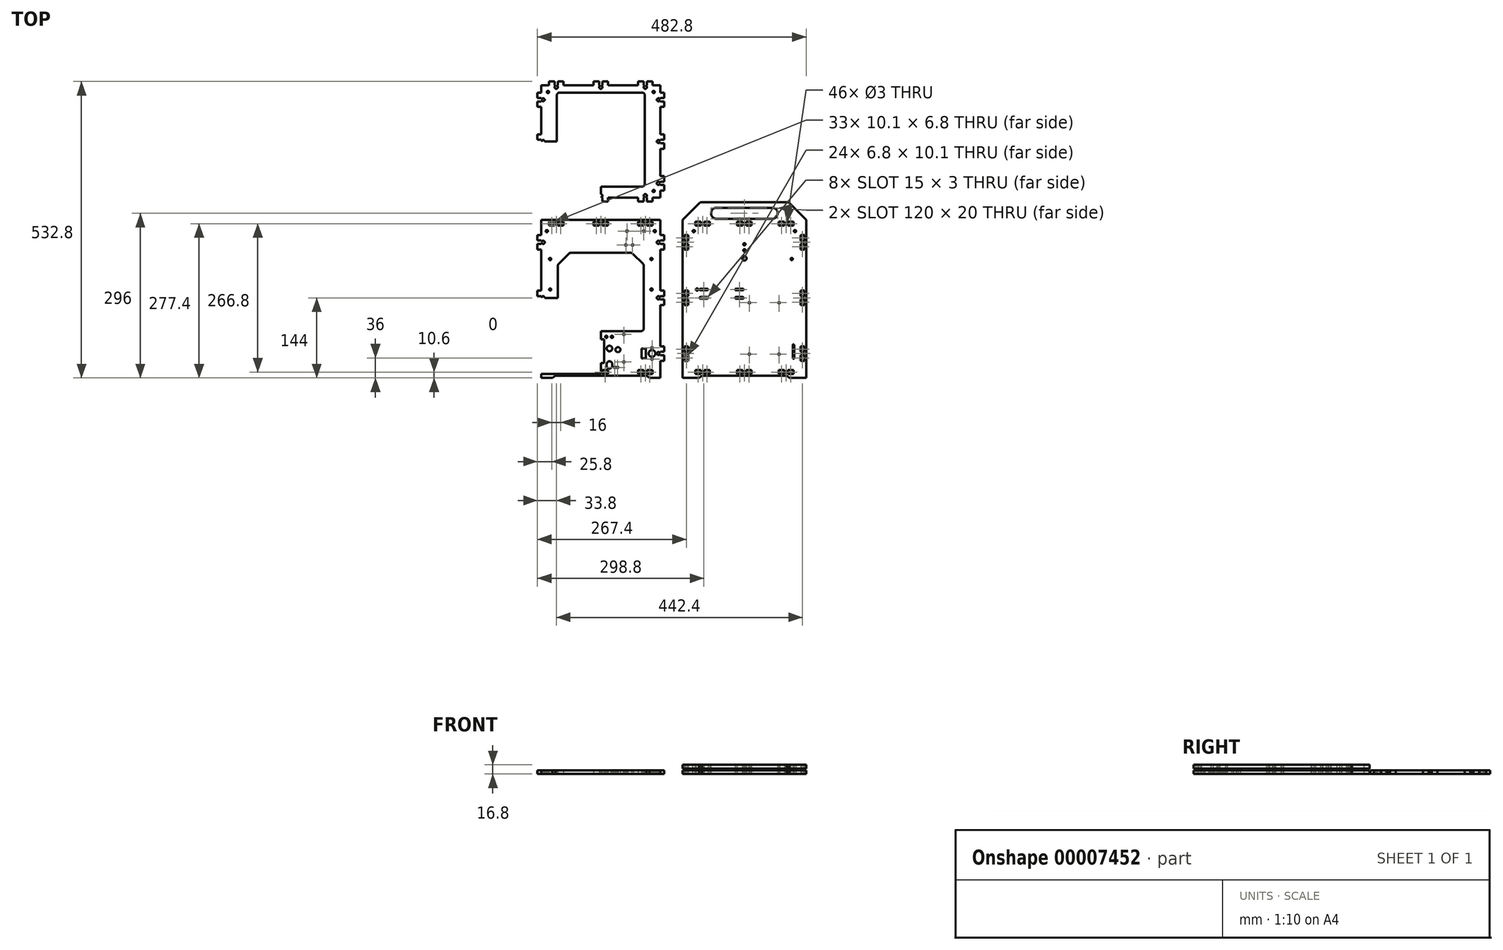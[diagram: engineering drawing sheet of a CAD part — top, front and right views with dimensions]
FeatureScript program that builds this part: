
annotation { "Feature Type Name" : "Feature", "Feature Type Description" : "" }
export const myFeature = defineFeature(function(context is Context, id is Id, definition is map)
    precondition{}
    {
        {
            var Q0;
            Q0=qCreatedBy(makeId("Top.planeOp"),FACE);
            var sketch = newSketch(context, id + "F0", { "sketchPlane" : qUnion([Q0])});
            skLineSegment(sketch, "E0", {"start": v(0, 0) * mm, "end": v(0, -101) * mm});
            skLineSegment(sketch, "E1", {"start": v(0, -101) * mm, "end": v(107, -101) * mm, "construction": true});
            skLineSegment(sketch, "E2", {"start": v(107, -101) * mm, "end": v(107, 101) * mm, "construction": true});
            skLineSegment(sketch, "E3", {"start": v(107, 101) * mm, "end": v(0, 101) * mm, "construction": true});
            skLineSegment(sketch, "E4", {"start": v(0, 101) * mm, "end": v(0, 0) * mm});
            skLineSegment(sketch, "E5", {"start": v(0, 0) * mm, "end": v(107, 0) * mm});
            skLineSegment(sketch, "E6", {"start": v(0, -101) * mm, "end": v(0, -151) * mm, "construction": true});
            skLineSegment(sketch, "E7", {"start": v(0, -151) * mm, "end": v(107, -151) * mm, "construction": true});
            skLineSegment(sketch, "E8", {"start": v(107, -151) * mm, "end": v(107, -411) * mm, "construction": true});
            skLineSegment(sketch, "E9", {"start": v(107, -411) * mm, "end": v(0, -411) * mm, "construction": true});
            skLineSegment(sketch, "E10", {"start": v(0, -411) * mm, "end": v(0, -151) * mm});
            skLineSegment(sketch, "E11", {"start": v(107, -151) * mm, "end": v(157, -151) * mm, "construction": true});
            skLineSegment(sketch, "E12", {"start": v(157, -151) * mm, "end": v(157, -411) * mm, "construction": true});
            skLineSegment(sketch, "E13", {"start": v(157, -411) * mm, "end": v(359, -411) * mm, "construction": true});
            skLineSegment(sketch, "E14", {"start": v(359, -411) * mm, "end": v(359, -151) * mm, "construction": true});
            skLineSegment(sketch, "E15", {"start": v(359, -151) * mm, "end": v(157, -151) * mm, "construction": true});
            skLineSegment(sketch, "E16", {"start": v(258, -151) * mm, "end": v(258, -411) * mm});
            skLineSegment(sketch, "E17", {"start": v(107, 0) * mm, "end": v(157, 0) * mm, "construction": true});
            skLineSegment(sketch, "E18", {"start": v(157, 0) * mm, "end": v(153.3, 0) * mm, "construction": true});
            skLineSegment(sketch, "E19", {"start": v(153.3, 0) * mm, "end": v(150.8, 0) * mm, "construction": true});
            skLineSegment(sketch, "E20", {"start": v(150.8, 0) * mm, "end": v(150.8, 1.5) * mm});
            skLineSegment(sketch, "E21", {"start": v(150.8, 1.5) * mm, "end": v(157, 1.5) * mm});
            skLineSegment(sketch, "E22", {"start": v(157, 1.5) * mm, "end": v(157, 3) * mm});
            skLineSegment(sketch, "E23", {"start": v(157, 3) * mm, "end": v(163.8, 3) * mm});
            skLineSegment(sketch, "E24", {"start": v(163.8, 3) * mm, "end": v(163.8, 13) * mm});
            skLineSegment(sketch, "E25", {"start": v(163.8, 13) * mm, "end": v(157, 13) * mm});
            skLineSegment(sketch, "E26.rect.bottom", {"start": v(154.5, 2.75) * mm, "end": v(152.1, 2.75) * mm});
            skLineSegment(sketch, "E26.rect.top", {"start": v(154.5, -2.75) * mm, "end": v(152.1, -2.75) * mm});
            skLineSegment(sketch, "E26.rect.left", {"start": v(154.5, 2.75) * mm, "end": v(154.5, -2.75) * mm});
            skLineSegment(sketch, "E26.rect.right", {"start": v(152.1, 2.75) * mm, "end": v(152.1, -2.75) * mm});
            skPoint(sketch, "E26.rect.middle", {"position": v(153.3, 0) * mm});
            skCircle(sketch, "E27", {"center": v(154.5, 2.75) * mm, "radius": 0.25 * mm});
            skLineSegment(sketch, "E28", {"start": v(157, 0) * mm, "end": v(187, 0) * mm, "construction": true});
            skLineSegment(sketch, "E29", {"start": v(187, 0) * mm, "end": v(187, 2.95) * mm, "construction": true});
            skLineSegment(sketch, "E30", {"start": v(187, 2.95) * mm, "end": v(193.8, 2.95) * mm});
            skLineSegment(sketch, "E31", {"start": v(193.8, 2.95) * mm, "end": v(193.8, 13.05) * mm});
            skLineSegment(sketch, "E32", {"start": v(193.8, 13.05) * mm, "end": v(187, 13.05) * mm});
            skLineSegment(sketch, "E33", {"start": v(187, 13.05) * mm, "end": v(187, 2.95) * mm});
            skLineSegment(sketch, "E34", {"start": v(187, 0) * mm, "end": v(190.4, 0) * mm, "construction": true});
            skLineSegment(sketch, "E35", {"start": v(190.4, 0) * mm, "end": v(190.4, 2.95) * mm, "construction": true});
            skCircle(sketch, "E36", {"center": v(190.4, 0) * mm, "radius": 1.5 * mm});
            skLineSegment(sketch, "E37", {"start": v(107, 0) * mm, "end": v(103.3, 0) * mm, "construction": true});
            skLineSegment(sketch, "E38", {"start": v(103.3, 0) * mm, "end": v(100.8, 0) * mm, "construction": true});
            skLineSegment(sketch, "E39", {"start": v(100.8, 0) * mm, "end": v(100.8, 1.5) * mm});
            skLineSegment(sketch, "E40", {"start": v(100.8, 1.5) * mm, "end": v(107, 1.5) * mm});
            skLineSegment(sketch, "E41", {"start": v(107, 1.5) * mm, "end": v(107, 3) * mm});
            skLineSegment(sketch, "E42", {"start": v(107, 3) * mm, "end": v(113.8, 3) * mm});
            skLineSegment(sketch, "E43", {"start": v(113.8, 3) * mm, "end": v(113.8, 13) * mm});
            skLineSegment(sketch, "E44", {"start": v(113.8, 13) * mm, "end": v(107, 13) * mm});
            skLineSegment(sketch, "E45.rect.bottom", {"start": v(104.5, 2.75) * mm, "end": v(102.1, 2.75) * mm});
            skLineSegment(sketch, "E45.rect.top", {"start": v(104.5, -2.75) * mm, "end": v(102.1, -2.75) * mm});
            skLineSegment(sketch, "E45.rect.left", {"start": v(104.5, 2.75) * mm, "end": v(104.5, -2.75) * mm});
            skLineSegment(sketch, "E45.rect.right", {"start": v(102.1, 2.75) * mm, "end": v(102.1, -2.75) * mm});
            skPoint(sketch, "E45.rect.middle", {"position": v(103.3, 0) * mm});
            skCircle(sketch, "E46", {"center": v(104.5, 2.75) * mm, "radius": 0.25 * mm});
            skLineSegment(sketch, "E47.0.MirrorCS", {"start": v(100.8, 0) * mm, "end": v(100.8, -1.5) * mm});
            skLineSegment(sketch, "E47.1.MirrorCS", {"start": v(107, -1.5) * mm, "end": v(107, -3) * mm});
            skCircle(sketch, "E47.2.MirrorC", {"center": v(104.5, -2.75) * mm, "radius": 0.25 * mm});
            skLineSegment(sketch, "E47.4.MirrorCS", {"start": v(113.8, -13) * mm, "end": v(107, -13) * mm});
            skLineSegment(sketch, "E47.6.MirrorCS", {"start": v(107, -3) * mm, "end": v(113.8, -3) * mm});
            skLineSegment(sketch, "E47.7.MirrorCS", {"start": v(100.8, -1.5) * mm, "end": v(107, -1.5) * mm});
            skLineSegment(sketch, "E47.8.MirrorCS", {"start": v(113.8, -3) * mm, "end": v(113.8, -13) * mm});
            skLineSegment(sketch, "E48", {"start": v(0, 101) * mm, "end": v(0, 97.3) * mm, "construction": true});
            skLineSegment(sketch, "E49", {"start": v(0, 97.3) * mm, "end": v(0, 94.8) * mm, "construction": true});
            skLineSegment(sketch, "E50", {"start": v(0, 94.8) * mm, "end": v(1.5, 94.8) * mm});
            skLineSegment(sketch, "E51", {"start": v(1.5, 94.8) * mm, "end": v(1.5, 101) * mm});
            skLineSegment(sketch, "E52", {"start": v(1.5, 101) * mm, "end": v(3, 101) * mm});
            skLineSegment(sketch, "E53", {"start": v(3, 101) * mm, "end": v(3, 107.8) * mm});
            skLineSegment(sketch, "E54", {"start": v(3, 107.8) * mm, "end": v(13, 107.8) * mm});
            skLineSegment(sketch, "E55", {"start": v(13, 107.8) * mm, "end": v(13, 101) * mm});
            skLineSegment(sketch, "E56.rect.bottom", {"start": v(2.75, 96.1) * mm, "end": v(-2.75, 96.1) * mm});
            skLineSegment(sketch, "E56.rect.top", {"start": v(2.75, 98.5) * mm, "end": v(-2.75, 98.5) * mm});
            skLineSegment(sketch, "E56.rect.left", {"start": v(2.75, 96.1) * mm, "end": v(2.75, 98.5) * mm});
            skLineSegment(sketch, "E56.rect.right", {"start": v(-2.75, 96.1) * mm, "end": v(-2.75, 98.5) * mm});
            skPoint(sketch, "E56.rect.middle", {"position": v(0, 97.3) * mm});
            skCircle(sketch, "E57", {"center": v(2.75, 98.5) * mm, "radius": 0.25 * mm});
            skLineSegment(sketch, "E58.0.MirrorCS", {"start": v(0, 94.8) * mm, "end": v(-1.5, 94.8) * mm});
            skCircle(sketch, "E58.1.MirrorC", {"center": v(-2.75, 98.5) * mm, "radius": 0.25 * mm});
            skLineSegment(sketch, "E58.3.MirrorCS", {"start": v(-1.5, 94.8) * mm, "end": v(-1.5, 101) * mm});
            skLineSegment(sketch, "E58.4.MirrorCS", {"start": v(-1.5, 101) * mm, "end": v(-3, 101) * mm});
            skLineSegment(sketch, "E58.5.MirrorCS", {"start": v(-3, 101) * mm, "end": v(-3, 107.8) * mm});
            skLineSegment(sketch, "E58.6.MirrorCS", {"start": v(-3, 107.8) * mm, "end": v(-13, 107.8) * mm});
            skLineSegment(sketch, "E58.7.MirrorCS", {"start": v(-13, 107.8) * mm, "end": v(-13, 101) * mm});
            skLineSegment(sketch, "E59", {"start": v(0, -281) * mm, "end": v(107, -281) * mm});
            skLineSegment(sketch, "E60", {"start": v(2.95, -151) * mm, "end": v(2.95, -144.2) * mm});
            skLineSegment(sketch, "E61", {"start": v(2.95, -144.2) * mm, "end": v(13.05, -144.2) * mm});
            skLineSegment(sketch, "E62", {"start": v(13.05, -144.2) * mm, "end": v(13.05, -151) * mm});
            skLineSegment(sketch, "E63", {"start": v(13.05, -151) * mm, "end": v(2.95, -151) * mm});
            skLineSegment(sketch, "E64", {"start": v(2.95, -147.6) * mm, "end": v(0, -147.6) * mm, "construction": true});
            skCircle(sketch, "E65", {"center": v(0, -147.6) * mm, "radius": 1.5 * mm});
            skLineSegment(sketch, "E66.0.MirrorCS", {"start": v(-13.05, -144.2) * mm, "end": v(-13.05, -151) * mm});
            skLineSegment(sketch, "E66.1.MirrorCS", {"start": v(-2.95, -151) * mm, "end": v(-2.95, -144.2) * mm});
            skLineSegment(sketch, "E66.2.MirrorCS", {"start": v(-13.05, -151) * mm, "end": v(-2.95, -151) * mm});
            skLineSegment(sketch, "E66.3.MirrorCS", {"start": v(-2.95, -144.2) * mm, "end": v(-13.05, -144.2) * mm});
            skLineSegment(sketch, "E67", {"start": v(260.95, -151) * mm, "end": v(260.95, -144.2) * mm});
            skLineSegment(sketch, "E68", {"start": v(260.95, -144.2) * mm, "end": v(271.05, -144.2) * mm});
            skLineSegment(sketch, "E69", {"start": v(271.05, -144.2) * mm, "end": v(271.05, -151) * mm});
            skLineSegment(sketch, "E70", {"start": v(271.05, -151) * mm, "end": v(260.95, -151) * mm});
            skLineSegment(sketch, "E71", {"start": v(260.95, -147.6) * mm, "end": v(258, -147.6) * mm, "construction": true});
            skLineSegment(sketch, "E72", {"start": v(258, -147.6) * mm, "end": v(258, -151) * mm, "construction": true});
            skCircle(sketch, "E73", {"center": v(258, -147.6) * mm, "radius": 1.5 * mm});
            skLineSegment(sketch, "E74.0.MirrorCS", {"start": v(244.95, -151) * mm, "end": v(255.05, -151) * mm});
            skLineSegment(sketch, "E74.1.MirrorCS", {"start": v(244.95, -144.2) * mm, "end": v(244.95, -151) * mm});
            skLineSegment(sketch, "E74.2.MirrorCS", {"start": v(255.05, -144.2) * mm, "end": v(244.95, -144.2) * mm});
            skLineSegment(sketch, "E74.3.MirrorCS", {"start": v(255.05, -151) * mm, "end": v(255.05, -144.2) * mm});
            skLineSegment(sketch, "E75", {"start": v(258, -281) * mm, "end": v(359, -281) * mm});
            skLineSegment(sketch, "E76", {"start": v(359, -278.05) * mm, "end": v(365.8, -278.05) * mm});
            skLineSegment(sketch, "E77", {"start": v(365.8, -278.05) * mm, "end": v(365.8, -267.95) * mm});
            skLineSegment(sketch, "E78", {"start": v(365.8, -267.95) * mm, "end": v(359, -267.95) * mm});
            skLineSegment(sketch, "E79", {"start": v(359, -267.95) * mm, "end": v(359, -278.05) * mm});
            skLineSegment(sketch, "E80", {"start": v(362.4, -278.05) * mm, "end": v(362.4, -281) * mm, "construction": true});
            skLineSegment(sketch, "E81", {"start": v(362.4, -281) * mm, "end": v(359, -281) * mm, "construction": true});
            skCircle(sketch, "E82", {"center": v(362.4, -281) * mm, "radius": 1.5 * mm});
            skLineSegment(sketch, "E83.0.MirrorCS", {"start": v(359, -294.05) * mm, "end": v(359, -283.95) * mm});
            skLineSegment(sketch, "E83.1.MirrorCS", {"start": v(359, -283.95) * mm, "end": v(365.8, -283.95) * mm});
            skLineSegment(sketch, "E83.2.MirrorCS", {"start": v(365.8, -294.05) * mm, "end": v(359, -294.05) * mm});
            skLineSegment(sketch, "E83.3.MirrorCS", {"start": v(365.8, -283.95) * mm, "end": v(365.8, -294.05) * mm});
            skLineSegment(sketch, "E84", {"start": v(107, -281) * mm, "end": v(103.3, -281) * mm, "construction": true});
            skLineSegment(sketch, "E85", {"start": v(103.3, -281) * mm, "end": v(100.8, -281) * mm, "construction": true});
            skLineSegment(sketch, "E86", {"start": v(100.8, -281) * mm, "end": v(100.8, -279.5) * mm});
            skLineSegment(sketch, "E87", {"start": v(100.8, -279.5) * mm, "end": v(107, -279.5) * mm});
            skLineSegment(sketch, "E88", {"start": v(107, -279.5) * mm, "end": v(107, -278) * mm});
            skLineSegment(sketch, "E89", {"start": v(107, -278) * mm, "end": v(113.8, -278) * mm});
            skLineSegment(sketch, "E90", {"start": v(113.8, -278) * mm, "end": v(113.8, -268) * mm});
            skLineSegment(sketch, "E91", {"start": v(113.8, -268) * mm, "end": v(107, -268) * mm});
            skLineSegment(sketch, "E92.rect.bottom", {"start": v(102.1, -278.25) * mm, "end": v(104.5, -278.25) * mm});
            skLineSegment(sketch, "E92.rect.top", {"start": v(102.1, -283.75) * mm, "end": v(104.5, -283.75) * mm});
            skLineSegment(sketch, "E92.rect.left", {"start": v(102.1, -278.25) * mm, "end": v(102.1, -283.75) * mm});
            skLineSegment(sketch, "E92.rect.right", {"start": v(104.5, -278.25) * mm, "end": v(104.5, -283.75) * mm});
            skPoint(sketch, "E92.rect.middle", {"position": v(103.3, -281) * mm});
            skCircle(sketch, "E93", {"center": v(104.5, -278.25) * mm, "radius": 0.25 * mm});
            skLineSegment(sketch, "E94.0.MirrorCS", {"start": v(100.8, -281) * mm, "end": v(100.8, -282.5) * mm});
            skCircle(sketch, "E94.1.MirrorC", {"center": v(104.5, -283.75) * mm, "radius": 0.25 * mm});
            skLineSegment(sketch, "E94.2.MirrorCS", {"start": v(100.8, -282.5) * mm, "end": v(107, -282.5) * mm});
            skLineSegment(sketch, "E94.4.MirrorCS", {"start": v(107, -284) * mm, "end": v(113.8, -284) * mm});
            skLineSegment(sketch, "E94.5.MirrorCS", {"start": v(113.8, -284) * mm, "end": v(113.8, -294) * mm});
            skLineSegment(sketch, "E94.6.MirrorCS", {"start": v(113.8, -294) * mm, "end": v(107, -294) * mm});
            skLineSegment(sketch, "E94.7.MirrorCS", {"start": v(107, -282.5) * mm, "end": v(107, -284) * mm});
            skLineSegment(sketch, "E95.1.0.0", {"start": v(83, 107.8) * mm, "end": v(93, 107.8) * mm});
            skPoint(sketch, "E95.1.0.1", {"position": v(80, 97.3) * mm});
            skLineSegment(sketch, "E95.1.0.2", {"start": v(77, 107.8) * mm, "end": v(67, 107.8) * mm});
            skLineSegment(sketch, "E95.1.0.3", {"start": v(93, 107.8) * mm, "end": v(93, 101) * mm});
            skLineSegment(sketch, "E95.1.0.4", {"start": v(67, 107.8) * mm, "end": v(67, 101) * mm});
            skLineSegment(sketch, "E95.1.0.5", {"start": v(83, 101) * mm, "end": v(83, 107.8) * mm});
            skLineSegment(sketch, "E95.1.0.6", {"start": v(77, 101) * mm, "end": v(77, 107.8) * mm});
            skLineSegment(sketch, "E95.1.0.7", {"start": v(80, 94.8) * mm, "end": v(78.5, 94.8) * mm});
            skLineSegment(sketch, "E95.1.0.8", {"start": v(78.5, 94.8) * mm, "end": v(78.5, 101) * mm});
            skLineSegment(sketch, "E95.1.0.9", {"start": v(82.75, 96.1) * mm, "end": v(77.25, 96.1) * mm});
            skLineSegment(sketch, "E95.1.0.10", {"start": v(80, 94.8) * mm, "end": v(81.5, 94.8) * mm});
            skLineSegment(sketch, "E95.1.0.11", {"start": v(81.5, 94.8) * mm, "end": v(81.5, 101) * mm});
            skLineSegment(sketch, "E95.1.0.12", {"start": v(77.25, 96.1) * mm, "end": v(77.25, 98.5) * mm});
            skLineSegment(sketch, "E95.1.0.13", {"start": v(82.75, 98.5) * mm, "end": v(77.25, 98.5) * mm});
            skLineSegment(sketch, "E95.1.0.14", {"start": v(78.5, 101) * mm, "end": v(77, 101) * mm});
            skLineSegment(sketch, "E95.1.0.15", {"start": v(80, 97.3) * mm, "end": v(80, 94.8) * mm, "construction": true});
            skLineSegment(sketch, "E95.1.0.16", {"start": v(81.5, 101) * mm, "end": v(83, 101) * mm});
            skLineSegment(sketch, "E95.1.0.17", {"start": v(77.25, 96.1) * mm, "end": v(77.25, 98.5) * mm});
            skCircle(sketch, "E95.1.0.18", {"center": v(82.75, 98.5) * mm, "radius": 0.25 * mm});
            skLineSegment(sketch, "E95.1.0.19", {"start": v(82.75, 96.1) * mm, "end": v(82.75, 98.5) * mm});
            skCircle(sketch, "E95.1.0.20", {"center": v(77.25, 98.5) * mm, "radius": 0.25 * mm});
            skLineSegment(sketch, "E95.1.0.21", {"start": v(80, 101) * mm, "end": v(80, 97.3) * mm, "construction": true});
            skLineSegment(sketch, "E95.direction1", {"start": v(3, 107.8) * mm, "end": v(83, 107.8) * mm, "construction": true});
            skLineSegment(sketch, "E96.0.1.0", {"start": v(113.8, 62) * mm, "end": v(107, 62) * mm});
            skPoint(sketch, "E96.0.1.1", {"position": v(103.3, 75) * mm});
            skLineSegment(sketch, "E96.0.1.2", {"start": v(113.8, 72) * mm, "end": v(113.8, 62) * mm});
            skLineSegment(sketch, "E96.0.1.3", {"start": v(107, 78) * mm, "end": v(113.8, 78) * mm});
            skLineSegment(sketch, "E96.0.1.4", {"start": v(107, 72) * mm, "end": v(113.8, 72) * mm});
            skLineSegment(sketch, "E96.0.1.5", {"start": v(113.8, 88) * mm, "end": v(107, 88) * mm});
            skLineSegment(sketch, "E96.0.1.6", {"start": v(113.8, 78) * mm, "end": v(113.8, 88) * mm});
            skPoint(sketch, "E96.0.1.7", {"position": v(103.3, 75) * mm});
            skLineSegment(sketch, "E96.0.1.8", {"start": v(107, 75) * mm, "end": v(103.3, 75) * mm, "construction": true});
            skLineSegment(sketch, "E96.0.1.9", {"start": v(104.5, 77.75) * mm, "end": v(104.5, 72.25) * mm});
            skLineSegment(sketch, "E96.0.1.10", {"start": v(100.8, 73.5) * mm, "end": v(107, 73.5) * mm});
            skLineSegment(sketch, "E96.0.1.11", {"start": v(100.8, 76.5) * mm, "end": v(107, 76.5) * mm});
            skLineSegment(sketch, "E96.0.1.12", {"start": v(107, 76.5) * mm, "end": v(107, 78) * mm});
            skLineSegment(sketch, "E96.0.1.13", {"start": v(100.8, 75) * mm, "end": v(100.8, 76.5) * mm});
            skCircle(sketch, "E96.0.1.14", {"center": v(104.5, 77.75) * mm, "radius": 0.25 * mm});
            skLineSegment(sketch, "E96.0.1.15", {"start": v(104.5, 77.75) * mm, "end": v(102.1, 77.75) * mm});
            skLineSegment(sketch, "E96.0.1.16", {"start": v(102.1, 77.75) * mm, "end": v(102.1, 72.25) * mm});
            skLineSegment(sketch, "E96.0.1.17", {"start": v(100.8, 75) * mm, "end": v(100.8, 73.5) * mm});
            skLineSegment(sketch, "E96.0.1.18", {"start": v(104.5, 72.25) * mm, "end": v(102.1, 72.25) * mm});
            skLineSegment(sketch, "E96.0.1.19", {"start": v(104.5, 72.25) * mm, "end": v(102.1, 72.25) * mm});
            skCircle(sketch, "E96.0.1.20", {"center": v(104.5, 72.25) * mm, "radius": 0.25 * mm});
            skLineSegment(sketch, "E96.0.1.21", {"start": v(103.3, 75) * mm, "end": v(100.8, 75) * mm, "construction": true});
            skLineSegment(sketch, "E96.0.1.22", {"start": v(107, 73.5) * mm, "end": v(107, 72) * mm});
            skLineSegment(sketch, "E96.direction1", {"start": v(107, -13) * mm, "end": v(132, -13) * mm, "construction": true});
            skLineSegment(sketch, "E96.direction2", {"start": v(107, -13) * mm, "end": v(107, 62) * mm, "construction": true});
            skLineSegment(sketch, "E97.1.0.0", {"start": v(66.95, -144.2) * mm, "end": v(66.95, -151) * mm});
            skLineSegment(sketch, "E97.1.0.1", {"start": v(66.95, -151) * mm, "end": v(77.05, -151) * mm});
            skLineSegment(sketch, "E97.1.0.2", {"start": v(77.05, -151) * mm, "end": v(77.05, -144.2) * mm});
            skLineSegment(sketch, "E97.1.0.3", {"start": v(77.05, -144.2) * mm, "end": v(66.95, -144.2) * mm});
            skCircle(sketch, "E97.1.0.4", {"center": v(80, -147.6) * mm, "radius": 1.5 * mm});
            skLineSegment(sketch, "E97.1.0.5", {"start": v(82.95, -144.2) * mm, "end": v(93.05, -144.2) * mm});
            skLineSegment(sketch, "E97.1.0.6", {"start": v(82.95, -151) * mm, "end": v(82.95, -144.2) * mm});
            skLineSegment(sketch, "E97.1.0.7", {"start": v(93.05, -151) * mm, "end": v(82.95, -151) * mm});
            skLineSegment(sketch, "E97.1.0.8", {"start": v(93.05, -144.2) * mm, "end": v(93.05, -151) * mm});
            skLineSegment(sketch, "E97.1.0.9", {"start": v(82.95, -147.6) * mm, "end": v(80, -147.6) * mm, "construction": true});
            skLineSegment(sketch, "E97.direction1", {"start": v(-13.05, -151) * mm, "end": v(66.95, -151) * mm, "construction": true});
            skPoint(sketch, "E98.0.1.0", {"position": v(103.3, -181) * mm});
            skLineSegment(sketch, "E98.0.1.1", {"start": v(113.8, -178) * mm, "end": v(113.8, -168) * mm});
            skLineSegment(sketch, "E98.0.1.2", {"start": v(113.8, -184) * mm, "end": v(113.8, -194) * mm});
            skLineSegment(sketch, "E98.0.1.3", {"start": v(113.8, -194) * mm, "end": v(107, -194) * mm});
            skLineSegment(sketch, "E98.0.1.4", {"start": v(113.8, -168) * mm, "end": v(107, -168) * mm});
            skPoint(sketch, "E98.0.1.5", {"position": v(103.3, -181) * mm});
            skLineSegment(sketch, "E98.0.1.6", {"start": v(107, -184) * mm, "end": v(113.8, -184) * mm});
            skLineSegment(sketch, "E98.0.1.7", {"start": v(107, -178) * mm, "end": v(113.8, -178) * mm});
            skLineSegment(sketch, "E98.0.1.8", {"start": v(102.1, -178.25) * mm, "end": v(104.5, -178.25) * mm});
            skLineSegment(sketch, "E98.0.1.9", {"start": v(104.5, -178.25) * mm, "end": v(104.5, -183.75) * mm});
            skLineSegment(sketch, "E98.0.1.10", {"start": v(100.8, -179.5) * mm, "end": v(107, -179.5) * mm});
            skLineSegment(sketch, "E98.0.1.11", {"start": v(100.8, -182.5) * mm, "end": v(107, -182.5) * mm});
            skLineSegment(sketch, "E98.0.1.12", {"start": v(107, -179.5) * mm, "end": v(107, -178) * mm});
            skLineSegment(sketch, "E98.0.1.13", {"start": v(107, -182.5) * mm, "end": v(107, -184) * mm});
            skLineSegment(sketch, "E98.0.1.14", {"start": v(107, -181) * mm, "end": v(103.3, -181) * mm, "construction": true});
            skLineSegment(sketch, "E98.0.1.15", {"start": v(102.1, -183.75) * mm, "end": v(104.5, -183.75) * mm});
            skCircle(sketch, "E98.0.1.16", {"center": v(104.5, -183.75) * mm, "radius": 0.25 * mm});
            skLineSegment(sketch, "E98.0.1.17", {"start": v(102.1, -178.25) * mm, "end": v(102.1, -183.75) * mm});
            skLineSegment(sketch, "E98.0.1.18", {"start": v(100.8, -181) * mm, "end": v(100.8, -182.5) * mm});
            skLineSegment(sketch, "E98.0.1.19", {"start": v(102.1, -183.75) * mm, "end": v(104.5, -183.75) * mm});
            skLineSegment(sketch, "E98.0.1.20", {"start": v(100.8, -181) * mm, "end": v(100.8, -179.5) * mm});
            skCircle(sketch, "E98.0.1.21", {"center": v(104.5, -178.25) * mm, "radius": 0.25 * mm});
            skLineSegment(sketch, "E98.0.1.22", {"start": v(103.3, -181) * mm, "end": v(100.8, -181) * mm, "construction": true});
            skLineSegment(sketch, "E98.direction1", {"start": v(103.3, -281) * mm, "end": v(128.76, -281) * mm, "construction": true});
            skLineSegment(sketch, "E98.direction2", {"start": v(103.3, -281) * mm, "end": v(103.3, -181) * mm, "construction": true});
            skLineSegment(sketch, "E99.1.0.0", {"start": v(346.05, -151) * mm, "end": v(335.95, -151) * mm});
            skLineSegment(sketch, "E99.1.0.1", {"start": v(335.95, -144.2) * mm, "end": v(346.05, -144.2) * mm});
            skLineSegment(sketch, "E99.1.0.2", {"start": v(319.95, -151) * mm, "end": v(330.05, -151) * mm});
            skLineSegment(sketch, "E99.1.0.3", {"start": v(330.05, -144.2) * mm, "end": v(319.95, -144.2) * mm});
            skLineSegment(sketch, "E99.1.0.4", {"start": v(346.05, -144.2) * mm, "end": v(346.05, -151) * mm});
            skLineSegment(sketch, "E99.1.0.5", {"start": v(319.95, -144.2) * mm, "end": v(319.95, -151) * mm});
            skLineSegment(sketch, "E99.1.0.6", {"start": v(330.05, -151) * mm, "end": v(330.05, -144.2) * mm});
            skLineSegment(sketch, "E99.1.0.7", {"start": v(335.95, -151) * mm, "end": v(335.95, -144.2) * mm});
            skCircle(sketch, "E99.1.0.8", {"center": v(333, -147.6) * mm, "radius": 1.5 * mm});
            skLineSegment(sketch, "E99.1.0.9", {"start": v(333, -147.6) * mm, "end": v(333, -151) * mm, "construction": true});
            skLineSegment(sketch, "E99.1.0.10", {"start": v(335.95, -147.6) * mm, "end": v(333, -147.6) * mm, "construction": true});
            skLineSegment(sketch, "E99.direction1", {"start": v(260.95, -151) * mm, "end": v(335.95, -151) * mm, "construction": true});
            skLineSegment(sketch, "E100.0.1.0", {"start": v(359, -167.95) * mm, "end": v(359, -178.05) * mm});
            skLineSegment(sketch, "E100.0.1.1", {"start": v(365.8, -178.05) * mm, "end": v(365.8, -167.95) * mm});
            skLineSegment(sketch, "E100.0.1.2", {"start": v(365.8, -167.95) * mm, "end": v(359, -167.95) * mm});
            skLineSegment(sketch, "E100.0.1.3", {"start": v(365.8, -194.05) * mm, "end": v(359, -194.05) * mm});
            skLineSegment(sketch, "E100.0.1.4", {"start": v(365.8, -183.95) * mm, "end": v(365.8, -194.05) * mm});
            skLineSegment(sketch, "E100.0.1.5", {"start": v(359, -194.05) * mm, "end": v(359, -183.95) * mm});
            skLineSegment(sketch, "E100.0.1.6", {"start": v(359, -178.05) * mm, "end": v(365.8, -178.05) * mm});
            skCircle(sketch, "E100.0.1.7", {"center": v(362.4, -181) * mm, "radius": 1.5 * mm});
            skLineSegment(sketch, "E100.0.1.8", {"start": v(362.4, -181) * mm, "end": v(359, -181) * mm, "construction": true});
            skLineSegment(sketch, "E100.0.1.9", {"start": v(359, -183.95) * mm, "end": v(365.8, -183.95) * mm});
            skLineSegment(sketch, "E100.0.1.10", {"start": v(362.4, -178.05) * mm, "end": v(362.4, -181) * mm, "construction": true});
            skLineSegment(sketch, "E100.direction1", {"start": v(359, -278.05) * mm, "end": v(459.05, -278.05) * mm, "construction": true});
            skLineSegment(sketch, "E100.direction2", {"start": v(359, -278.05) * mm, "end": v(359, -178.05) * mm, "construction": true});
            skLineSegment(sketch, "E101", {"start": v(107, -268) * mm, "end": v(107, -194) * mm});
            skLineSegment(sketch, "E102", {"start": v(107, -168) * mm, "end": v(107, -151) * mm});
            skLineSegment(sketch, "E103", {"start": v(107, -151) * mm, "end": v(107, -141) * mm});
            skLineSegment(sketch, "E104", {"start": v(107, -141) * mm, "end": v(0, -141) * mm});
            skLineSegment(sketch, "E105", {"start": v(0, -141) * mm, "end": v(0, -151) * mm});
            skLineSegment(sketch, "E106", {"start": v(359, -281) * mm, "end": v(369, -281) * mm});
            skLineSegment(sketch, "E107", {"start": v(369, -281) * mm, "end": v(369, -141) * mm});
            skLineSegment(sketch, "E108", {"start": v(369, -141) * mm, "end": v(258, -141) * mm});
            skLineSegment(sketch, "E109", {"start": v(258, -141) * mm, "end": v(258, -151) * mm});
            skLineSegment(sketch, "E110", {"start": v(13, 101) * mm, "end": v(67, 101) * mm});
            skLineSegment(sketch, "E111", {"start": v(93, 101) * mm, "end": v(107, 101) * mm});
            skLineSegment(sketch, "E112", {"start": v(107, 101) * mm, "end": v(107, 88) * mm});
            skLineSegment(sketch, "E113", {"start": v(107, 62) * mm, "end": v(107, 13) * mm});
            skLineSegment(sketch, "E114.0.MirrorCS", {"start": v(-107, -411) * mm, "end": v(0, -411) * mm, "construction": true});
            skLineSegment(sketch, "E114.1.MirrorCS", {"start": v(0, -151) * mm, "end": v(-107, -151) * mm, "construction": true});
            skLineSegment(sketch, "E114.2.MirrorCS", {"start": v(-107, -151) * mm, "end": v(-107, -411) * mm, "construction": true});
            skSolve(sketch);
        }
        {
            var Q0;
            Q0=qCreatedBy(makeId("Top.planeOp"),FACE);
            var sketch = newSketch(context, id + "F1", { "sketchPlane" : qUnion([Q0])});
            skLineSegment(sketch, "E115.0", {"start": v(0, -151) * mm, "end": v(-107, -151) * mm});
            skLineSegment(sketch, "E116.0", {"start": v(0, -151) * mm, "end": v(107, -151) * mm});
            skLineSegment(sketch, "E117.0", {"start": v(107, -151) * mm, "end": v(107, -411) * mm});
            skLineSegment(sketch, "E118.0", {"start": v(107, -411) * mm, "end": v(0, -411) * mm});
            skLineSegment(sketch, "E119.0", {"start": v(-107, -411) * mm, "end": v(0, -411) * mm});
            skLineSegment(sketch, "E120.0", {"start": v(-107, -151) * mm, "end": v(-107, -411) * mm});
            skLineSegment(sketch, "E121.0", {"start": v(157, -151) * mm, "end": v(157, -411) * mm});
            skLineSegment(sketch, "E122.0", {"start": v(157, -411) * mm, "end": v(359, -411) * mm});
            skLineSegment(sketch, "E123.0", {"start": v(359, -411) * mm, "end": v(359, -151) * mm});
            skLineSegment(sketch, "E124.0", {"start": v(359, -151) * mm, "end": v(157, -151) * mm});
            skLineSegment(sketch, "E125.0", {"start": v(0, -101) * mm, "end": v(107, -101) * mm});
            skLineSegment(sketch, "E126.0", {"start": v(107, -101) * mm, "end": v(107, 101) * mm});
            skLineSegment(sketch, "E127.0", {"start": v(107, 101) * mm, "end": v(0, 101) * mm});
            skLineSegment(sketch, "E128", {"start": v(258, -151) * mm, "end": v(258, -139) * mm});
            skLineSegment(sketch, "E129", {"start": v(258, -139) * mm, "end": v(308, -139) * mm});
            skLineSegment(sketch, "E130", {"start": v(308, -139) * mm, "end": v(308, -119) * mm});
            skLineSegment(sketch, "E131", {"start": v(308, -119) * mm, "end": v(258, -119) * mm});
            skLineSegment(sketch, "E132", {"start": v(258, -119) * mm, "end": v(258, -109) * mm});
            skLineSegment(sketch, "E133", {"start": v(258, -109) * mm, "end": v(334.93, -109) * mm});
            skLineSegment(sketch, "E134.0", {"start": v(369, -281) * mm, "end": v(369, -141) * mm});
            skLineSegment(sketch, "E135", {"start": v(338.46, -110.46) * mm, "end": v(369, -141) * mm});
            skLineSegment(sketch, "E136", {"start": v(369, -281) * mm, "end": v(369, -425) * mm});
            skLineSegment(sketch, "E137", {"start": v(369, -425) * mm, "end": v(339, -425) * mm});
            skLineSegment(sketch, "E138", {"start": v(339, -425) * mm, "end": v(334, -421) * mm});
            skLineSegment(sketch, "E139", {"start": v(334, -421) * mm, "end": v(258, -421) * mm});
            skLineSegment(sketch, "E140", {"start": v(258, -411) * mm, "end": v(258, -421) * mm});
            skLineSegment(sketch, "E141", {"start": v(0, -411) * mm, "end": v(0, -421) * mm});
            skLineSegment(sketch, "E142", {"start": v(0, -421) * mm, "end": v(82, -421) * mm});
            skLineSegment(sketch, "E143", {"start": v(82, -421) * mm, "end": v(87, -425) * mm});
            skLineSegment(sketch, "E144", {"start": v(87, -425) * mm, "end": v(107, -425) * mm});
            skLineSegment(sketch, "E145", {"start": v(107, -425) * mm, "end": v(107, -411) * mm});
            skLineSegment(sketch, "E146", {"start": v(107, -425) * mm, "end": v(369, -425) * mm, "construction": true});
            skLineSegment(sketch, "E147", {"start": v(0, -421) * mm, "end": v(258, -421) * mm, "construction": true});
            skLineSegment(sketch, "E148.0.MirrorCS", {"start": v(-82, -421) * mm, "end": v(-87, -425) * mm});
            skLineSegment(sketch, "E148.1.MirrorCS", {"start": v(0, -421) * mm, "end": v(-82, -421) * mm});
            skLineSegment(sketch, "E148.2.MirrorCS", {"start": v(-107, -425) * mm, "end": v(-107, -411) * mm});
            skLineSegment(sketch, "E148.3.MirrorCS", {"start": v(-87, -425) * mm, "end": v(-107, -425) * mm});
            skArc(sketch, "E149", {"start": v(308, -139) * mm, "mid": v(318, -129) * mm, "end": v(308, -119) * mm});
            skLineSegment(sketch, "E150.0.MirrorCS", {"start": v(182, -421) * mm, "end": v(258, -421) * mm});
            skLineSegment(sketch, "E150.1.MirrorCS", {"start": v(177, -425) * mm, "end": v(182, -421) * mm});
            skLineSegment(sketch, "E150.2.MirrorCS", {"start": v(147, -425) * mm, "end": v(177, -425) * mm});
            skLineSegment(sketch, "E150.3.MirrorCS", {"start": v(147, -281) * mm, "end": v(147, -425) * mm});
            skLineSegment(sketch, "E150.4.MirrorCS", {"start": v(177.54, -110.46) * mm, "end": v(147, -141) * mm});
            skLineSegment(sketch, "E150.5.MirrorCS", {"start": v(258, -109) * mm, "end": v(181.07, -109) * mm});
            skLineSegment(sketch, "E150.6.MirrorCS", {"start": v(208, -119) * mm, "end": v(258, -119) * mm});
            skLineSegment(sketch, "E150.7.MirrorCS", {"start": v(258, -139) * mm, "end": v(208, -139) * mm});
            skArc(sketch, "E150.8.MirrorCS", {"start": v(208, -139) * mm, "mid": v(198, -129) * mm, "end": v(208, -119) * mm});
            skLineSegment(sketch, "E151", {"start": v(147, -281) * mm, "end": v(147, -141) * mm});
            skLineSegment(sketch, "E152.0", {"start": v(260.95, -144.2) * mm, "end": v(271.05, -144.2) * mm});
            skLineSegment(sketch, "E153.0", {"start": v(365.8, -278.05) * mm, "end": v(365.8, -267.95) * mm});
            skLineSegment(sketch, "E154", {"start": v(258, -144.2) * mm, "end": v(365.8, -144.2) * mm});
            skLineSegment(sketch, "E155", {"start": v(365.8, -144.2) * mm, "end": v(365.8, -281) * mm});
            skLineSegment(sketch, "E156.0", {"start": v(258, -281) * mm, "end": v(359, -281) * mm});
            skLineSegment(sketch, "E157.0.MirrorCS", {"start": v(150.2, -144.2) * mm, "end": v(150.2, -281) * mm});
            skLineSegment(sketch, "E157.1.MirrorCS", {"start": v(258, -144.2) * mm, "end": v(150.2, -144.2) * mm});
            skLineSegment(sketch, "E158.0.MirrorCS", {"start": v(365.8, -417.8) * mm, "end": v(365.8, -281) * mm});
            skLineSegment(sketch, "E158.1.MirrorCS", {"start": v(258, -417.8) * mm, "end": v(365.8, -417.8) * mm});
            skLineSegment(sketch, "E158.2.MirrorCS", {"start": v(150.2, -417.8) * mm, "end": v(150.2, -281) * mm});
            skLineSegment(sketch, "E158.3.MirrorCS", {"start": v(258, -417.8) * mm, "end": v(150.2, -417.8) * mm});
            skLineSegment(sketch, "E159.0", {"start": v(2.95, -144.2) * mm, "end": v(13.05, -144.2) * mm});
            skLineSegment(sketch, "E160", {"start": v(0, -144.2) * mm, "end": v(107, -144.2) * mm});
            skLineSegment(sketch, "E161.0", {"start": v(0, -281) * mm, "end": v(107, -281) * mm});
            skLineSegment(sketch, "E162", {"start": v(107, -144.2) * mm, "end": v(107, -151) * mm});
            skLineSegment(sketch, "E163", {"start": v(107, -411) * mm, "end": v(107, -417.8) * mm});
            skLineSegment(sketch, "E164", {"start": v(107, -417.8) * mm, "end": v(-107, -417.8) * mm});
            skPoint(sketch, "E165.visualSharp", {"position": v(147, -141) * mm});
            skPoint(sketch, "E166.visualSharp", {"position": v(179, -109) * mm});
            skArc(sketch, "E166.filletArc", {"start": v(181.07, -109) * mm, "mid": v(179.16, -109.38) * mm, "end": v(177.54, -110.46) * mm});
            skPoint(sketch, "E167.visualSharp", {"position": v(337, -109) * mm});
            skArc(sketch, "E167.filletArc", {"start": v(338.46, -110.46) * mm, "mid": v(336.84, -109.38) * mm, "end": v(334.93, -109) * mm});
            skPoint(sketch, "E168.visualSharp", {"position": v(369, -141) * mm});
            skSolve(sketch);
        }
        {
            var Q0;
            Q0=qCreatedBy(makeId("Top.planeOp"),FACE);
            var sketch = newSketch(context, id + "F2", { "sketchPlane" : qUnion([Q0])});
            skLineSegment(sketch, "E169.rect.bottom", {"start": v(74, 88) * mm, "end": v(-74, 88) * mm});
            skLineSegment(sketch, "E169.rect.top", {"start": v(74, -81) * mm, "end": v(-74, -81) * mm});
            skLineSegment(sketch, "E169.rect.left", {"start": v(79, 83) * mm, "end": v(79, -76) * mm});
            skLineSegment(sketch, "E169.rect.right", {"start": v(-79, 83) * mm, "end": v(-79, -76) * mm});
            skPoint(sketch, "E169.rect.middle", {"position": v(0, 3.5) * mm});
            skCircle(sketch, "E170", {"center": v(30, -243) * mm, "radius": 1.5 * mm});
            skCircle(sketch, "E171", {"center": v(25, -406) * mm, "radius": 1.5 * mm});
            skCircle(sketch, "E172", {"center": v(30, -406) * mm, "radius": 1.5 * mm});
            skCircle(sketch, "E173", {"center": v(97, -161) * mm, "radius": 2 * mm});
            skCircle(sketch, "E174", {"center": v(95, -89) * mm, "radius": 2 * mm});
            skCircle(sketch, "E175", {"center": v(95, 89) * mm, "radius": 2 * mm});
            skCircle(sketch, "E176", {"center": v(167, -161) * mm, "radius": 2 * mm});
            skCircle(sketch, "E177", {"center": v(349, -161) * mm, "radius": 2 * mm});
            skCircle(sketch, "E178", {"center": v(173, -266) * mm, "radius": 2 * mm});
            skCircle(sketch, "E179", {"center": v(343, -211.2) * mm, "radius": 2 * mm});
            skLineSegment(sketch, "E180", {"start": v(179, -282.5) * mm, "end": v(179, -279.5) * mm});
            skLineSegment(sketch, "E181", {"start": v(179, -279.5) * mm, "end": v(191, -279.5) * mm});
            skLineSegment(sketch, "E182", {"start": v(191, -279.5) * mm, "end": v(191, -282.5) * mm});
            skLineSegment(sketch, "E183", {"start": v(191, -282.5) * mm, "end": v(179, -282.5) * mm});
            skArc(sketch, "E184", {"start": v(179, -279.5) * mm, "mid": v(177.5, -281) * mm, "end": v(179, -282.5) * mm});
            skArc(sketch, "E185", {"start": v(191, -282.5) * mm, "mid": v(192.5, -281) * mm, "end": v(191, -279.5) * mm});
            skLineSegment(sketch, "E186.0", {"start": v(0, 101) * mm, "end": v(0, 0) * mm});
            skCircle(sketch, "E187.0.MirrorC", {"center": v(-95, -89) * mm, "radius": 2 * mm});
            skCircle(sketch, "E187.1.MirrorC", {"center": v(-95, 89) * mm, "radius": 2 * mm});
            skCircle(sketch, "E188", {"center": v(91, -266) * mm, "radius": 2 * mm});
            skLineSegment(sketch, "E189", {"start": v(91, -266) * mm, "end": v(173, -266) * mm, "construction": true});
            skArc(sketch, "E190.0.1.0", {"start": v(191, -267.5) * mm, "mid": v(192.5, -266) * mm, "end": v(191, -264.5) * mm});
            skLineSegment(sketch, "E190.0.1.1", {"start": v(191, -267.5) * mm, "end": v(179, -267.5) * mm});
            skLineSegment(sketch, "E190.0.1.2", {"start": v(179, -264.5) * mm, "end": v(191, -264.5) * mm});
            skLineSegment(sketch, "E190.0.1.3", {"start": v(179, -267.5) * mm, "end": v(179, -264.5) * mm});
            skArc(sketch, "E190.0.1.4", {"start": v(179, -264.5) * mm, "mid": v(177.5, -266) * mm, "end": v(179, -267.5) * mm});
            skLineSegment(sketch, "E190.0.1.5", {"start": v(191, -264.5) * mm, "end": v(191, -267.5) * mm});
            skArc(sketch, "E190.1.0.0", {"start": v(255, -282.5) * mm, "mid": v(256.5, -281) * mm, "end": v(255, -279.5) * mm});
            skLineSegment(sketch, "E190.1.0.1", {"start": v(255, -282.5) * mm, "end": v(243, -282.5) * mm});
            skLineSegment(sketch, "E190.1.0.2", {"start": v(243, -279.5) * mm, "end": v(255, -279.5) * mm});
            skLineSegment(sketch, "E190.1.0.3", {"start": v(243, -282.5) * mm, "end": v(243, -279.5) * mm});
            skArc(sketch, "E190.1.0.4", {"start": v(243, -279.5) * mm, "mid": v(241.5, -281) * mm, "end": v(243, -282.5) * mm});
            skLineSegment(sketch, "E190.1.0.5", {"start": v(255, -279.5) * mm, "end": v(255, -282.5) * mm});
            skArc(sketch, "E190.1.1.0", {"start": v(255, -267.5) * mm, "mid": v(256.5, -266) * mm, "end": v(255, -264.5) * mm});
            skLineSegment(sketch, "E190.1.1.1", {"start": v(255, -267.5) * mm, "end": v(243, -267.5) * mm});
            skLineSegment(sketch, "E190.1.1.2", {"start": v(243, -264.5) * mm, "end": v(255, -264.5) * mm});
            skLineSegment(sketch, "E190.1.1.3", {"start": v(243, -267.5) * mm, "end": v(243, -264.5) * mm});
            skArc(sketch, "E190.1.1.4", {"start": v(243, -264.5) * mm, "mid": v(241.5, -266) * mm, "end": v(243, -267.5) * mm});
            skLineSegment(sketch, "E190.1.1.5", {"start": v(255, -264.5) * mm, "end": v(255, -267.5) * mm});
            skLineSegment(sketch, "E190.direction1", {"start": v(191, -282.5) * mm, "end": v(255, -282.5) * mm, "construction": true});
            skLineSegment(sketch, "E190.direction2", {"start": v(191, -282.5) * mm, "end": v(191, -267.5) * mm, "construction": true});
            skCircle(sketch, "E191.0.MirrorC", {"center": v(-25, -406) * mm, "radius": 1.5 * mm});
            skCircle(sketch, "E191.1.MirrorC", {"center": v(-30, -406) * mm, "radius": 1.5 * mm});
            skCircle(sketch, "E191.2.MirrorC", {"center": v(-30, -243) * mm, "radius": 1.5 * mm});
            skCircle(sketch, "E192.0.MirrorC", {"center": v(-97, -161) * mm, "radius": 2 * mm});
            skCircle(sketch, "E192.1.MirrorC", {"center": v(-91, -266) * mm, "radius": 2 * mm});
            skLineSegment(sketch, "E193", {"start": v(173, -266) * mm, "end": v(179, -266) * mm, "construction": true});
            skLineSegment(sketch, "E194", {"start": v(263.04, -285.92) * mm, "end": v(263.04, -386) * mm, "construction": true});
            skLineSegment(sketch, "E195", {"start": v(263.04, -285.92) * mm, "end": v(324, -285.92) * mm, "construction": true});
            skLineSegment(sketch, "E196", {"start": v(324, -285.92) * mm, "end": v(324, -386) * mm, "construction": true});
            skLineSegment(sketch, "E197", {"start": v(324, -386) * mm, "end": v(263.04, -386) * mm, "construction": true});
            skLineSegment(sketch, "E198", {"start": v(266.85, -289.73) * mm, "end": v(266.85, -382.19) * mm, "construction": true});
            skLineSegment(sketch, "E199", {"start": v(266.85, -382.19) * mm, "end": v(320.2, -382.19) * mm, "construction": true});
            skLineSegment(sketch, "E200", {"start": v(320.2, -382.19) * mm, "end": v(320.2, -289.73) * mm, "construction": true});
            skLineSegment(sketch, "E201", {"start": v(320.2, -289.73) * mm, "end": v(266.85, -289.73) * mm, "construction": true});
            skCircle(sketch, "E202", {"center": v(266.85, -382.19) * mm, "radius": 1.5 * mm});
            skCircle(sketch, "E203", {"center": v(266.85, -289.73) * mm, "radius": 1.5 * mm});
            skCircle(sketch, "E204", {"center": v(320.2, -289.73) * mm, "radius": 1.5 * mm});
            skCircle(sketch, "E205", {"center": v(320.2, -382.19) * mm, "radius": 1.5 * mm});
            skLineSegment(sketch, "E206", {"start": v(92, -371) * mm, "end": v(92, -391) * mm, "construction": true});
            skCircle(sketch, "E207", {"center": v(92, -381) * mm, "radius": 6 * mm});
            skCircle(sketch, "E208", {"center": v(92, -371) * mm, "radius": 1.5 * mm});
            skCircle(sketch, "E209", {"center": v(92, -391) * mm, "radius": 1.5 * mm});
            skLineSegment(sketch, "E210.rect.bottom", {"start": v(81, -372) * mm, "end": v(73, -372) * mm});
            skLineSegment(sketch, "E210.rect.top", {"start": v(81, -390) * mm, "end": v(73, -390) * mm});
            skLineSegment(sketch, "E210.rect.left", {"start": v(81, -372) * mm, "end": v(81, -390) * mm});
            skLineSegment(sketch, "E210.rect.right", {"start": v(73, -372) * mm, "end": v(73, -390) * mm});
            skPoint(sketch, "E210.rect.middle", {"position": v(77, -381) * mm});
            skLineSegment(sketch, "E211", {"start": v(77, -381) * mm, "end": v(92, -381) * mm, "construction": true});
            skLineSegment(sketch, "E212.0", {"start": v(0, -411) * mm, "end": v(0, -151) * mm});
            skLineSegment(sketch, "E213", {"start": v(0, -411) * mm, "end": v(15.5, -411) * mm, "construction": true});
            skLineSegment(sketch, "E214", {"start": v(15.5, -411) * mm, "end": v(15.5, -403) * mm, "construction": true});
            skLineSegment(sketch, "E215", {"start": v(15.5, -403) * mm, "end": v(15.5, -372) * mm, "construction": true});
            skCircle(sketch, "E216", {"center": v(15.5, -372) * mm, "radius": 5 * mm});
            skCircle(sketch, "E217.0.MirrorC", {"center": v(-15.5, -372) * mm, "radius": 5 * mm});
            skCircle(sketch, "E218", {"center": v(10, -351) * mm, "radius": 2 * mm});
            skLineSegment(sketch, "E219", {"start": v(0, -351) * mm, "end": v(10, -351) * mm, "construction": true});
            skLineSegment(sketch, "E220", {"start": v(10, -351) * mm, "end": v(20, -351) * mm, "construction": true});
            skCircle(sketch, "E221", {"center": v(20, -351) * mm, "radius": 2 * mm});
            skCircle(sketch, "E222.0.MirrorC", {"center": v(-20, -351) * mm, "radius": 2 * mm});
            skCircle(sketch, "E222.1.MirrorC", {"center": v(-10, -351) * mm, "radius": 2 * mm});
            skLineSegment(sketch, "E223", {"start": v(10.5, -403) * mm, "end": v(20.5, -403) * mm});
            skLineSegment(sketch, "E224", {"start": v(20.5, -403) * mm, "end": v(20.5, -400) * mm});
            skLineSegment(sketch, "E225", {"start": v(20.5, -400) * mm, "end": v(10.5, -400) * mm});
            skLineSegment(sketch, "E226", {"start": v(10.5, -400) * mm, "end": v(10.5, -403) * mm});
            skArc(sketch, "E227", {"start": v(10.5, -403) * mm, "mid": v(15.5, -408) * mm, "end": v(20.5, -403) * mm});
            skArc(sketch, "E228", {"start": v(20.5, -400) * mm, "mid": v(15.5, -395) * mm, "end": v(10.5, -400) * mm});
            skLineSegment(sketch, "E229.0.MirrorCS", {"start": v(-20.5, -403) * mm, "end": v(-20.5, -400) * mm});
            skLineSegment(sketch, "E229.1.MirrorCS", {"start": v(-10.5, -400) * mm, "end": v(-10.5, -403) * mm});
            skArc(sketch, "E229.2.MirrorCS", {"start": v(-10.5, -403) * mm, "mid": v(-15.5, -408) * mm, "end": v(-20.5, -403) * mm});
            skArc(sketch, "E229.3.MirrorCS", {"start": v(-20.5, -400) * mm, "mid": v(-15.5, -395) * mm, "end": v(-10.5, -400) * mm});
            skLineSegment(sketch, "E230.0", {"start": v(258, -151) * mm, "end": v(258, -411) * mm});
            skCircle(sketch, "E231", {"center": v(258, -184.6) * mm, "radius": 2 * mm});
            skCircle(sketch, "E232", {"center": v(258, -195.4) * mm, "radius": 2 * mm});
            skCircle(sketch, "E233", {"center": v(258, -210) * mm, "radius": 4 * mm});
            skLineSegment(sketch, "E234.rect.bottom", {"start": v(15.5, -253) * mm, "end": v(-15.5, -253) * mm});
            skLineSegment(sketch, "E234.rect.top", {"start": v(15.5, -288) * mm, "end": v(-15.5, -288) * mm});
            skLineSegment(sketch, "E234.rect.left", {"start": v(15.5, -253) * mm, "end": v(15.5, -288) * mm});
            skLineSegment(sketch, "E234.rect.right", {"start": v(-15.5, -253) * mm, "end": v(-15.5, -288) * mm});
            skPoint(sketch, "E234.rect.middle", {"position": v(0, -270.5) * mm});
            skLineSegment(sketch, "E235", {"start": v(47, -161) * mm, "end": v(77, -161) * mm, "construction": true});
            skCircle(sketch, "E236", {"center": v(47, -161) * mm, "radius": 1.5 * mm});
            skCircle(sketch, "E237", {"center": v(77, -161) * mm, "radius": 1.5 * mm});
            skArc(sketch, "E238", {"start": v(58, -266) * mm, "mid": v(51, -259) * mm, "end": v(44, -266) * mm});
            skPoint(sketch, "E239.visualSharp", {"position": v(-79, 88) * mm});
            skArc(sketch, "E239.filletArc", {"start": v(-74, 88) * mm, "mid": v(-77.54, 86.54) * mm, "end": v(-79, 83) * mm});
            skPoint(sketch, "E240.visualSharp", {"position": v(79, 88) * mm});
            skArc(sketch, "E240.filletArc", {"start": v(79, 83) * mm, "mid": v(77.54, 86.54) * mm, "end": v(74, 88) * mm});
            skPoint(sketch, "E241.visualSharp", {"position": v(79, -81) * mm});
            skArc(sketch, "E241.filletArc", {"start": v(74, -81) * mm, "mid": v(77.54, -79.54) * mm, "end": v(79, -76) * mm});
            skPoint(sketch, "E242.visualSharp", {"position": v(-79, -81) * mm});
            skArc(sketch, "E242.filletArc", {"start": v(-79, -76) * mm, "mid": v(-77.54, -79.54) * mm, "end": v(-74, -81) * mm});
            skLineSegment(sketch, "E243", {"start": v(91, -266) * mm, "end": v(51, -266) * mm, "construction": true});
            skLineSegment(sketch, "E244", {"start": v(51, -266) * mm, "end": v(51, -186) * mm, "construction": true});
            skLineSegment(sketch, "E245", {"start": v(45, -226) * mm, "end": v(57, -226) * mm, "construction": true});
            skLineSegment(sketch, "E246", {"start": v(45, -186) * mm, "end": v(57, -186) * mm, "construction": true});
            skPoint(sketch, "E247", {"position": v(51, -226) * mm});
            skCircle(sketch, "E248", {"center": v(45, -186) * mm, "radius": 1.5 * mm});
            skCircle(sketch, "E249", {"center": v(57, -186) * mm, "radius": 1.5 * mm});
            skCircle(sketch, "E250", {"center": v(57, -226) * mm, "radius": 1.5 * mm});
            skCircle(sketch, "E251", {"center": v(45, -226) * mm, "radius": 1.5 * mm});
            skLineSegment(sketch, "E252.bottom", {"start": v(58, -266) * mm, "end": v(51, -266) * mm});
            skLineSegment(sketch, "E252.left", {"start": v(58, -266) * mm, "end": v(58, -276) * mm});
            skLineSegment(sketch, "E252.right", {"start": v(44, -266) * mm, "end": v(44, -276) * mm});
            skPoint(sketch, "E252.middle", {"position": v(51, -271) * mm});
            skArc(sketch, "E253", {"start": v(44, -276) * mm, "mid": v(51, -283) * mm, "end": v(58, -276) * mm});
            skSolve(sketch);
        }
        {
            var Q0;
            Q0=qCreatedBy(makeId("Top.planeOp"),FACE);
            var sketch = newSketch(context, id + "F3", { "sketchPlane" : qUnion([Q0])});
            skCircle(sketch, "E254.0", {"center": v(97, -161) * mm, "radius": 2 * mm});
            skCircle(sketch, "E255.0", {"center": v(167, -161) * mm, "radius": 2 * mm});
            skCircle(sketch, "E256.0", {"center": v(349, -161) * mm, "radius": 2 * mm});
            skCircle(sketch, "E257.0", {"center": v(343, -211.2) * mm, "radius": 2 * mm});
            skArc(sketch, "E258.0", {"start": v(255, -267.5) * mm, "mid": v(256.5, -266) * mm, "end": v(255, -264.5) * mm});
            skLineSegment(sketch, "E259.0", {"start": v(243, -264.5) * mm, "end": v(255, -264.5) * mm});
            skLineSegment(sketch, "E260.0", {"start": v(255, -267.5) * mm, "end": v(243, -267.5) * mm});
            skArc(sketch, "E261.0", {"start": v(243, -264.5) * mm, "mid": v(241.5, -266) * mm, "end": v(243, -267.5) * mm});
            skLineSegment(sketch, "E262.0", {"start": v(243, -279.5) * mm, "end": v(255, -279.5) * mm});
            skArc(sketch, "E263.0", {"start": v(243, -279.5) * mm, "mid": v(241.5, -281) * mm, "end": v(243, -282.5) * mm});
            skArc(sketch, "E264.0", {"start": v(255, -282.5) * mm, "mid": v(256.5, -281) * mm, "end": v(255, -279.5) * mm});
            skLineSegment(sketch, "E265.0", {"start": v(255, -282.5) * mm, "end": v(243, -282.5) * mm});
            skArc(sketch, "E266.0", {"start": v(191, -267.5) * mm, "mid": v(192.5, -266) * mm, "end": v(191, -264.5) * mm});
            skLineSegment(sketch, "E267.0", {"start": v(191, -267.5) * mm, "end": v(179, -267.5) * mm});
            skLineSegment(sketch, "E268.0", {"start": v(179, -264.5) * mm, "end": v(191, -264.5) * mm});
            skArc(sketch, "E269.0", {"start": v(179, -264.5) * mm, "mid": v(177.5, -266) * mm, "end": v(179, -267.5) * mm});
            skArc(sketch, "E270.0", {"start": v(179, -279.5) * mm, "mid": v(177.5, -281) * mm, "end": v(179, -282.5) * mm});
            skLineSegment(sketch, "E271.0", {"start": v(179, -279.5) * mm, "end": v(191, -279.5) * mm});
            skLineSegment(sketch, "E272.0", {"start": v(191, -282.5) * mm, "end": v(179, -282.5) * mm});
            skArc(sketch, "E273.0", {"start": v(191, -282.5) * mm, "mid": v(192.5, -281) * mm, "end": v(191, -279.5) * mm});
            skCircle(sketch, "E274.0", {"center": v(173, -266) * mm, "radius": 2 * mm});
            skLineSegment(sketch, "E275.rect.top", {"start": v(72, -341) * mm, "end": v(-72, -341) * mm});
            skLineSegment(sketch, "E275.rect.left", {"start": v(77, -223.07) * mm, "end": v(77, -336) * mm});
            skLineSegment(sketch, "E275.rect.right", {"start": v(-77, -223.07) * mm, "end": v(-77, -336) * mm});
            skPoint(sketch, "E275.rect.middle", {"position": v(0, -281) * mm});
            skLineSegment(sketch, "E276", {"start": v(-92, -356.76) * mm, "end": v(-92, -396.76) * mm, "construction": true});
            skLineSegment(sketch, "E277", {"start": v(-92, -396.76) * mm, "end": v(5, -396.76) * mm, "construction": true});
            skLineSegment(sketch, "E278", {"start": v(5, -396.76) * mm, "end": v(5, -356.76) * mm, "construction": true});
            skLineSegment(sketch, "E279", {"start": v(5, -356.76) * mm, "end": v(-92, -356.76) * mm, "construction": true});
            skCircle(sketch, "E280.0", {"center": v(-97, -161) * mm, "radius": 2 * mm});
            skLineSegment(sketch, "E281", {"start": v(343, -211.2) * mm, "end": v(0, -211.2) * mm, "construction": true});
            skCircle(sketch, "E282", {"center": v(91, -211.2) * mm, "radius": 2 * mm});
            skLineSegment(sketch, "E283", {"start": v(0, 0) * mm, "end": v(0, -211.2) * mm, "construction": true});
            skCircle(sketch, "E284.0.MirrorC", {"center": v(-91, -211.2) * mm, "radius": 2 * mm});
            skCircle(sketch, "E285", {"center": v(25, 73) * mm, "radius": 1.5 * mm});
            skCircle(sketch, "E286", {"center": v(30, 36) * mm, "radius": 1.5 * mm});
            skCircle(sketch, "E287", {"center": v(47, 60) * mm, "radius": 1.5 * mm});
            skCircle(sketch, "E288", {"center": v(47, 43) * mm, "radius": 1.5 * mm});
            skCircle(sketch, "E289.0.MirrorC", {"center": v(-30, 36) * mm, "radius": 1.5 * mm});
            skCircle(sketch, "E289.1.MirrorC", {"center": v(-25, 73) * mm, "radius": 1.5 * mm});
            skLineSegment(sketch, "E290", {"start": v(-106, -344) * mm, "end": v(44.04, -344) * mm, "construction": true});
            skLineSegment(sketch, "E291", {"start": v(44.04, -344) * mm, "end": v(44.04, -399) * mm, "construction": true});
            skLineSegment(sketch, "E292", {"start": v(44.04, -399) * mm, "end": v(-106, -399) * mm, "construction": true});
            skLineSegment(sketch, "E293", {"start": v(-106, -399) * mm, "end": v(-106, -344) * mm, "construction": true});
            skCircle(sketch, "E294", {"center": v(-103.25, -346.66) * mm, "radius": 1.5 * mm});
            skLineSegment(sketch, "E295.bottom", {"start": v(-103.25, -346.66) * mm, "end": v(41.54, -346.66) * mm, "construction": true});
            skLineSegment(sketch, "E295.top", {"start": v(-103.25, -396.25) * mm, "end": v(41.54, -396.25) * mm, "construction": true});
            skLineSegment(sketch, "E295.left", {"start": v(-103.25, -346.66) * mm, "end": v(-103.25, -396.25) * mm, "construction": true});
            skLineSegment(sketch, "E295.right", {"start": v(41.54, -346.66) * mm, "end": v(41.54, -396.25) * mm, "construction": true});
            skCircle(sketch, "E296", {"center": v(-103.25, -396.25) * mm, "radius": 1.5 * mm});
            skCircle(sketch, "E297", {"center": v(41.54, -346.66) * mm, "radius": 1.5 * mm});
            skCircle(sketch, "E298", {"center": v(41.54, -396.25) * mm, "radius": 1.5 * mm});
            skLineSegment(sketch, "E299.bottom", {"start": v(-92.5, -347) * mm, "end": v(5.5, -347) * mm, "construction": true});
            skLineSegment(sketch, "E299.top", {"start": v(-92.5, -407.5) * mm, "end": v(5.5, -407.5) * mm, "construction": true});
            skLineSegment(sketch, "E299.left", {"start": v(-92.5, -347) * mm, "end": v(-92.5, -407.5) * mm, "construction": true});
            skLineSegment(sketch, "E299.right", {"start": v(5.5, -347) * mm, "end": v(5.5, -407.5) * mm, "construction": true});
            skCircle(sketch, "E300", {"center": v(30.74, -374.2) * mm, "radius": 4.5 * mm});
            skPoint(sketch, "E301.visualSharp", {"position": v(-77, -221) * mm});
            skPoint(sketch, "E302.visualSharp", {"position": v(77, -221) * mm});
            skPoint(sketch, "E303.visualSharp", {"position": v(77, -341) * mm});
            skArc(sketch, "E303.filletArc", {"start": v(72, -341) * mm, "mid": v(75.54, -339.54) * mm, "end": v(77, -336) * mm});
            skPoint(sketch, "E304.visualSharp", {"position": v(-77, -341) * mm});
            skArc(sketch, "E304.filletArc", {"start": v(-77, -336) * mm, "mid": v(-75.54, -339.54) * mm, "end": v(-72, -341) * mm});
            skLineSegment(sketch, "E305", {"start": v(347.4, -389) * mm, "end": v(347.4, -366) * mm});
            skLineSegment(sketch, "E306", {"start": v(347.4, -366) * mm, "end": v(344.8, -366) * mm});
            skLineSegment(sketch, "E307", {"start": v(344.8, -366) * mm, "end": v(344.8, -389) * mm});
            skLineSegment(sketch, "E308", {"start": v(344.8, -389) * mm, "end": v(347.4, -389) * mm});
            skArc(sketch, "E309", {"start": v(347.4, -366) * mm, "mid": v(346.1, -364.7) * mm, "end": v(344.8, -366) * mm});
            skArc(sketch, "E310", {"start": v(344.8, -389) * mm, "mid": v(346.1, -390.3) * mm, "end": v(347.4, -389) * mm});
            skLineSegment(sketch, "E311", {"start": v(347.4, -389) * mm, "end": v(347.4, -399) * mm, "construction": true});
            skLineSegment(sketch, "E312", {"start": v(44.04, -399) * mm, "end": v(347.4, -399) * mm, "construction": true});
            skLineSegment(sketch, "E313.bottom", {"start": v(-93, -355.76) * mm, "end": v(6, -355.76) * mm});
            skLineSegment(sketch, "E313.top", {"start": v(-93, -397.76) * mm, "end": v(6, -397.76) * mm});
            skLineSegment(sketch, "E313.left", {"start": v(-93, -355.76) * mm, "end": v(-93, -397.76) * mm});
            skLineSegment(sketch, "E313.right", {"start": v(6, -355.76) * mm, "end": v(6, -397.76) * mm});
            skLineSegment(sketch, "E314", {"start": v(0, -200.2) * mm, "end": v(54.13, -200.2) * mm});
            skLineSegment(sketch, "E315", {"start": v(57.66, -201.66) * mm, "end": v(75.54, -219.54) * mm});
            skLineSegment(sketch, "E316", {"start": v(0, -200.2) * mm, "end": v(-54.13, -200.2) * mm});
            skLineSegment(sketch, "E317", {"start": v(-57.66, -201.66) * mm, "end": v(-75.54, -219.54) * mm});
            skArc(sketch, "E318.filletArc", {"start": v(-75.54, -219.54) * mm, "mid": v(-76.62, -221.16) * mm, "end": v(-77, -223.07) * mm});
            skPoint(sketch, "E319.visualSharp", {"position": v(-56.2, -200.2) * mm});
            skArc(sketch, "E319.filletArc", {"start": v(-54.13, -200.2) * mm, "mid": v(-56.04, -200.58) * mm, "end": v(-57.66, -201.66) * mm});
            skPoint(sketch, "E320.visualSharp", {"position": v(56.2, -200.2) * mm});
            skArc(sketch, "E320.filletArc", {"start": v(57.66, -201.66) * mm, "mid": v(56.04, -200.58) * mm, "end": v(54.13, -200.2) * mm});
            skArc(sketch, "E321.filletArc", {"start": v(77, -223.07) * mm, "mid": v(76.62, -221.16) * mm, "end": v(75.54, -219.54) * mm});
            skCircle(sketch, "E322.0", {"center": v(258, -184.6) * mm, "radius": 2 * mm});
            skCircle(sketch, "E323.0", {"center": v(258, -195.4) * mm, "radius": 2 * mm});
            skCircle(sketch, "E324.0", {"center": v(258, -210) * mm, "radius": 4 * mm});
            skCircle(sketch, "E325", {"center": v(30.24, -354.5) * mm, "radius": 6.5 * mm, "construction": true});
            skPoint(sketch, "E326", {"position": v(347.4, -377.5) * mm});
            skSolve(sketch);
        }
        {
            var Q0;
            {var subQ29=sQuery(id+"F0.wireOp",EDGE,"E39");Q0=makeQuery(id+"F0.imprint","IMPRINT",FACE,{"disambiguationData":[TD([[makeQuery(id+"F0.imprint","IMPRINT",EDGE,{"derivedFrom":subQ29}),1.0]])]});}
            var Q1;
            Q1=makeQuery(id+"F0.imprint","IMPRINT",FACE,{"disambiguationData":[TD([[makeQuery(id+"F0.imprint","IMPRINT",EDGE,{"derivedFrom":sQuery(id+"F0.wireOp",EDGE,"E60")}),1.0]])]});
            var Q2;
            Q2=makeQuery(id+"F0.imprint","IMPRINT",FACE,{"disambiguationData":[TD([[makeQuery(id+"F0.imprint","IMPRINT",EDGE,{"derivedFrom":sQuery(id+"F0.wireOp",EDGE,"E67")}),1.0]])]});
            extrude(context, id + "F4", {"entities" : qUnion([Q0, Q1, Q2]), "depth" : 6.8 * mm});
        }
        {
            var Q0;
            Q0=makeQuery(id+"F4.opExtrude","SWEPT_BODY",BODY,{"disambiguationData":[OSD([sQuery(id+"F0.wireOp",EDGE,"E4"),sQuery(id+"F0.wireOp",EDGE,"E5"),sQuery(id+"F0.wireOp",EDGE,"E39"),sQuery(id+"F0.wireOp",EDGE,"E40"),sQuery(id+"F0.wireOp",EDGE,"E41"),sQuery(id+"F0.wireOp",EDGE,"E42"),sQuery(id+"F0.wireOp",EDGE,"E43"),sQuery(id+"F0.wireOp",EDGE,"E44"),sQuery(id+"F0.wireOp",EDGE,"E45.rect.bottom"),sQuery(id+"F0.wireOp",EDGE,"E45.rect.left"),sQuery(id+"F0.wireOp",EDGE,"E45.rect.right"),sQuery(id+"F0.wireOp",EDGE,"E46"),sQuery(id+"F0.wireOp",EDGE,"E50"),sQuery(id+"F0.wireOp",EDGE,"E51"),sQuery(id+"F0.wireOp",EDGE,"E52"),sQuery(id+"F0.wireOp",EDGE,"E53"),sQuery(id+"F0.wireOp",EDGE,"E54"),sQuery(id+"F0.wireOp",EDGE,"E55"),sQuery(id+"F0.wireOp",EDGE,"E56.rect.bottom"),sQuery(id+"F0.wireOp",EDGE,"E56.rect.top"),sQuery(id+"F0.wireOp",EDGE,"E56.rect.left"),sQuery(id+"F0.wireOp",EDGE,"E57"),sQuery(id+"F0.wireOp",EDGE,"E95.1.0.0"),sQuery(id+"F0.wireOp",EDGE,"E95.1.0.2"),sQuery(id+"F0.wireOp",EDGE,"E95.1.0.3"),sQuery(id+"F0.wireOp",EDGE,"E95.1.0.4"),sQuery(id+"F0.wireOp",EDGE,"E95.1.0.5"),sQuery(id+"F0.wireOp",EDGE,"E95.1.0.6"),sQuery(id+"F0.wireOp",EDGE,"E95.1.0.7"),sQuery(id+"F0.wireOp",EDGE,"E95.1.0.8"),sQuery(id+"F0.wireOp",EDGE,"E95.1.0.9"),sQuery(id+"F0.wireOp",EDGE,"E95.1.0.10"),sQuery(id+"F0.wireOp",EDGE,"E95.1.0.11"),sQuery(id+"F0.wireOp",EDGE,"E95.1.0.13"),sQuery(id+"F0.wireOp",EDGE,"E95.1.0.14"),sQuery(id+"F0.wireOp",EDGE,"E95.1.0.16"),sQuery(id+"F0.wireOp",EDGE,"E95.1.0.17"),sQuery(id+"F0.wireOp",EDGE,"E95.1.0.18"),sQuery(id+"F0.wireOp",EDGE,"E95.1.0.19"),sQuery(id+"F0.wireOp",EDGE,"E95.1.0.20"),sQuery(id+"F0.wireOp",EDGE,"E96.0.1.0"),sQuery(id+"F0.wireOp",EDGE,"E96.0.1.2"),sQuery(id+"F0.wireOp",EDGE,"E96.0.1.3"),sQuery(id+"F0.wireOp",EDGE,"E96.0.1.4"),sQuery(id+"F0.wireOp",EDGE,"E96.0.1.5"),sQuery(id+"F0.wireOp",EDGE,"E96.0.1.6"),sQuery(id+"F0.wireOp",EDGE,"E96.0.1.9"),sQuery(id+"F0.wireOp",EDGE,"E96.0.1.10"),sQuery(id+"F0.wireOp",EDGE,"E96.0.1.11"),sQuery(id+"F0.wireOp",EDGE,"E96.0.1.12"),sQuery(id+"F0.wireOp",EDGE,"E96.0.1.13"),sQuery(id+"F0.wireOp",EDGE,"E96.0.1.14"),sQuery(id+"F0.wireOp",EDGE,"E96.0.1.15"),sQuery(id+"F0.wireOp",EDGE,"E96.0.1.16"),sQuery(id+"F0.wireOp",EDGE,"E96.0.1.17"),sQuery(id+"F0.wireOp",EDGE,"E96.0.1.19"),sQuery(id+"F0.wireOp",EDGE,"E96.0.1.20"),sQuery(id+"F0.wireOp",EDGE,"E96.0.1.22"),sQuery(id+"F0.wireOp",EDGE,"E110"),sQuery(id+"F0.wireOp",EDGE,"E111"),sQuery(id+"F0.wireOp",EDGE,"E112"),sQuery(id+"F0.wireOp",EDGE,"E113")])]});
            var Q1;
            Q1=makeQuery(id+"F4.opExtrude","SWEPT_BODY",BODY,{"disambiguationData":[OSD([sQuery(id+"F0.wireOp",EDGE,"E10"),sQuery(id+"F0.wireOp",EDGE,"E59"),sQuery(id+"F0.wireOp",EDGE,"E60"),sQuery(id+"F0.wireOp",EDGE,"E61"),sQuery(id+"F0.wireOp",EDGE,"E62"),sQuery(id+"F0.wireOp",EDGE,"E63"),sQuery(id+"F0.wireOp",EDGE,"E65"),sQuery(id+"F0.wireOp",EDGE,"E86"),sQuery(id+"F0.wireOp",EDGE,"E87"),sQuery(id+"F0.wireOp",EDGE,"E88"),sQuery(id+"F0.wireOp",EDGE,"E89"),sQuery(id+"F0.wireOp",EDGE,"E90"),sQuery(id+"F0.wireOp",EDGE,"E91"),sQuery(id+"F0.wireOp",EDGE,"E92.rect.bottom"),sQuery(id+"F0.wireOp",EDGE,"E92.rect.left"),sQuery(id+"F0.wireOp",EDGE,"E92.rect.right"),sQuery(id+"F0.wireOp",EDGE,"E93"),sQuery(id+"F0.wireOp",EDGE,"E97.1.0.0"),sQuery(id+"F0.wireOp",EDGE,"E97.1.0.1"),sQuery(id+"F0.wireOp",EDGE,"E97.1.0.2"),sQuery(id+"F0.wireOp",EDGE,"E97.1.0.3"),sQuery(id+"F0.wireOp",EDGE,"E97.1.0.4"),sQuery(id+"F0.wireOp",EDGE,"E97.1.0.5"),sQuery(id+"F0.wireOp",EDGE,"E97.1.0.6"),sQuery(id+"F0.wireOp",EDGE,"E97.1.0.7"),sQuery(id+"F0.wireOp",EDGE,"E97.1.0.8"),sQuery(id+"F0.wireOp",EDGE,"E98.0.1.1"),sQuery(id+"F0.wireOp",EDGE,"E98.0.1.2"),sQuery(id+"F0.wireOp",EDGE,"E98.0.1.3"),sQuery(id+"F0.wireOp",EDGE,"E98.0.1.4"),sQuery(id+"F0.wireOp",EDGE,"E98.0.1.6"),sQuery(id+"F0.wireOp",EDGE,"E98.0.1.7"),sQuery(id+"F0.wireOp",EDGE,"E98.0.1.8"),sQuery(id+"F0.wireOp",EDGE,"E98.0.1.9"),sQuery(id+"F0.wireOp",EDGE,"E98.0.1.10"),sQuery(id+"F0.wireOp",EDGE,"E98.0.1.11"),sQuery(id+"F0.wireOp",EDGE,"E98.0.1.12"),sQuery(id+"F0.wireOp",EDGE,"E98.0.1.13"),sQuery(id+"F0.wireOp",EDGE,"E98.0.1.16"),sQuery(id+"F0.wireOp",EDGE,"E98.0.1.17"),sQuery(id+"F0.wireOp",EDGE,"E98.0.1.18"),sQuery(id+"F0.wireOp",EDGE,"E98.0.1.19"),sQuery(id+"F0.wireOp",EDGE,"E98.0.1.20"),sQuery(id+"F0.wireOp",EDGE,"E98.0.1.21"),sQuery(id+"F0.wireOp",EDGE,"E101"),sQuery(id+"F0.wireOp",EDGE,"E102"),sQuery(id+"F0.wireOp",EDGE,"E103"),sQuery(id+"F0.wireOp",EDGE,"E104"),sQuery(id+"F0.wireOp",EDGE,"E105")])]});
            var Q2;
            Q2=qCreatedBy(makeId("Right.planeOp"),FACE);
            mirror(context, id + "F5", {"operationType" : NewBodyOperationType.ADD, "entities" : qUnion([Q0, Q1]), "mirrorPlane" : qUnion([Q2])});
        }
        {
            var Q0;
            Q0=makeQuery(id+"F4.opExtrude","SWEPT_BODY",BODY,{"disambiguationData":[OSD([sQuery(id+"F0.wireOp",EDGE,"E4"),sQuery(id+"F0.wireOp",EDGE,"E5"),sQuery(id+"F0.wireOp",EDGE,"E39"),sQuery(id+"F0.wireOp",EDGE,"E40"),sQuery(id+"F0.wireOp",EDGE,"E41"),sQuery(id+"F0.wireOp",EDGE,"E42"),sQuery(id+"F0.wireOp",EDGE,"E43"),sQuery(id+"F0.wireOp",EDGE,"E44"),sQuery(id+"F0.wireOp",EDGE,"E45.rect.bottom"),sQuery(id+"F0.wireOp",EDGE,"E45.rect.left"),sQuery(id+"F0.wireOp",EDGE,"E45.rect.right"),sQuery(id+"F0.wireOp",EDGE,"E46"),sQuery(id+"F0.wireOp",EDGE,"E50"),sQuery(id+"F0.wireOp",EDGE,"E51"),sQuery(id+"F0.wireOp",EDGE,"E52"),sQuery(id+"F0.wireOp",EDGE,"E53"),sQuery(id+"F0.wireOp",EDGE,"E54"),sQuery(id+"F0.wireOp",EDGE,"E55"),sQuery(id+"F0.wireOp",EDGE,"E56.rect.bottom"),sQuery(id+"F0.wireOp",EDGE,"E56.rect.top"),sQuery(id+"F0.wireOp",EDGE,"E56.rect.left"),sQuery(id+"F0.wireOp",EDGE,"E57"),sQuery(id+"F0.wireOp",EDGE,"E95.1.0.0"),sQuery(id+"F0.wireOp",EDGE,"E95.1.0.2"),sQuery(id+"F0.wireOp",EDGE,"E95.1.0.3"),sQuery(id+"F0.wireOp",EDGE,"E95.1.0.4"),sQuery(id+"F0.wireOp",EDGE,"E95.1.0.5"),sQuery(id+"F0.wireOp",EDGE,"E95.1.0.6"),sQuery(id+"F0.wireOp",EDGE,"E95.1.0.7"),sQuery(id+"F0.wireOp",EDGE,"E95.1.0.8"),sQuery(id+"F0.wireOp",EDGE,"E95.1.0.9"),sQuery(id+"F0.wireOp",EDGE,"E95.1.0.10"),sQuery(id+"F0.wireOp",EDGE,"E95.1.0.11"),sQuery(id+"F0.wireOp",EDGE,"E95.1.0.13"),sQuery(id+"F0.wireOp",EDGE,"E95.1.0.14"),sQuery(id+"F0.wireOp",EDGE,"E95.1.0.16"),sQuery(id+"F0.wireOp",EDGE,"E95.1.0.17"),sQuery(id+"F0.wireOp",EDGE,"E95.1.0.18"),sQuery(id+"F0.wireOp",EDGE,"E95.1.0.19"),sQuery(id+"F0.wireOp",EDGE,"E95.1.0.20"),sQuery(id+"F0.wireOp",EDGE,"E96.0.1.0"),sQuery(id+"F0.wireOp",EDGE,"E96.0.1.2"),sQuery(id+"F0.wireOp",EDGE,"E96.0.1.3"),sQuery(id+"F0.wireOp",EDGE,"E96.0.1.4"),sQuery(id+"F0.wireOp",EDGE,"E96.0.1.5"),sQuery(id+"F0.wireOp",EDGE,"E96.0.1.6"),sQuery(id+"F0.wireOp",EDGE,"E96.0.1.9"),sQuery(id+"F0.wireOp",EDGE,"E96.0.1.10"),sQuery(id+"F0.wireOp",EDGE,"E96.0.1.11"),sQuery(id+"F0.wireOp",EDGE,"E96.0.1.12"),sQuery(id+"F0.wireOp",EDGE,"E96.0.1.13"),sQuery(id+"F0.wireOp",EDGE,"E96.0.1.14"),sQuery(id+"F0.wireOp",EDGE,"E96.0.1.15"),sQuery(id+"F0.wireOp",EDGE,"E96.0.1.16"),sQuery(id+"F0.wireOp",EDGE,"E96.0.1.17"),sQuery(id+"F0.wireOp",EDGE,"E96.0.1.19"),sQuery(id+"F0.wireOp",EDGE,"E96.0.1.20"),sQuery(id+"F0.wireOp",EDGE,"E96.0.1.22"),sQuery(id+"F0.wireOp",EDGE,"E110"),sQuery(id+"F0.wireOp",EDGE,"E111"),sQuery(id+"F0.wireOp",EDGE,"E112"),sQuery(id+"F0.wireOp",EDGE,"E113")])]});
            var Q1;
            Q1=qCreatedBy(makeId("Front.planeOp"),FACE);
            mirror(context, id + "F6", {"operationType" : NewBodyOperationType.ADD, "entities" : qUnion([Q0]), "mirrorPlane" : qUnion([Q1])});
        }
        {
            var Q0;
            Q0=makeQuery(id+"F4.opExtrude","SWEPT_BODY",BODY,{"disambiguationData":[OSD([sQuery(id+"F0.wireOp",EDGE,"E10"),sQuery(id+"F0.wireOp",EDGE,"E59"),sQuery(id+"F0.wireOp",EDGE,"E60"),sQuery(id+"F0.wireOp",EDGE,"E61"),sQuery(id+"F0.wireOp",EDGE,"E62"),sQuery(id+"F0.wireOp",EDGE,"E63"),sQuery(id+"F0.wireOp",EDGE,"E65"),sQuery(id+"F0.wireOp",EDGE,"E86"),sQuery(id+"F0.wireOp",EDGE,"E87"),sQuery(id+"F0.wireOp",EDGE,"E88"),sQuery(id+"F0.wireOp",EDGE,"E89"),sQuery(id+"F0.wireOp",EDGE,"E90"),sQuery(id+"F0.wireOp",EDGE,"E91"),sQuery(id+"F0.wireOp",EDGE,"E92.rect.bottom"),sQuery(id+"F0.wireOp",EDGE,"E92.rect.left"),sQuery(id+"F0.wireOp",EDGE,"E92.rect.right"),sQuery(id+"F0.wireOp",EDGE,"E93"),sQuery(id+"F0.wireOp",EDGE,"E97.1.0.0"),sQuery(id+"F0.wireOp",EDGE,"E97.1.0.1"),sQuery(id+"F0.wireOp",EDGE,"E97.1.0.2"),sQuery(id+"F0.wireOp",EDGE,"E97.1.0.3"),sQuery(id+"F0.wireOp",EDGE,"E97.1.0.4"),sQuery(id+"F0.wireOp",EDGE,"E97.1.0.5"),sQuery(id+"F0.wireOp",EDGE,"E97.1.0.6"),sQuery(id+"F0.wireOp",EDGE,"E97.1.0.7"),sQuery(id+"F0.wireOp",EDGE,"E97.1.0.8"),sQuery(id+"F0.wireOp",EDGE,"E98.0.1.1"),sQuery(id+"F0.wireOp",EDGE,"E98.0.1.2"),sQuery(id+"F0.wireOp",EDGE,"E98.0.1.3"),sQuery(id+"F0.wireOp",EDGE,"E98.0.1.4"),sQuery(id+"F0.wireOp",EDGE,"E98.0.1.6"),sQuery(id+"F0.wireOp",EDGE,"E98.0.1.7"),sQuery(id+"F0.wireOp",EDGE,"E98.0.1.8"),sQuery(id+"F0.wireOp",EDGE,"E98.0.1.9"),sQuery(id+"F0.wireOp",EDGE,"E98.0.1.10"),sQuery(id+"F0.wireOp",EDGE,"E98.0.1.11"),sQuery(id+"F0.wireOp",EDGE,"E98.0.1.12"),sQuery(id+"F0.wireOp",EDGE,"E98.0.1.13"),sQuery(id+"F0.wireOp",EDGE,"E98.0.1.16"),sQuery(id+"F0.wireOp",EDGE,"E98.0.1.17"),sQuery(id+"F0.wireOp",EDGE,"E98.0.1.18"),sQuery(id+"F0.wireOp",EDGE,"E98.0.1.19"),sQuery(id+"F0.wireOp",EDGE,"E98.0.1.20"),sQuery(id+"F0.wireOp",EDGE,"E98.0.1.21"),sQuery(id+"F0.wireOp",EDGE,"E101"),sQuery(id+"F0.wireOp",EDGE,"E102"),sQuery(id+"F0.wireOp",EDGE,"E103"),sQuery(id+"F0.wireOp",EDGE,"E104"),sQuery(id+"F0.wireOp",EDGE,"E105")])]});
            var Q1;
            Q1=makeQuery(id+"F4.opExtrude","SWEPT_BODY",BODY,{"disambiguationData":[OSD([sQuery(id+"F0.wireOp",EDGE,"E16"),sQuery(id+"F0.wireOp",EDGE,"E67"),sQuery(id+"F0.wireOp",EDGE,"E68"),sQuery(id+"F0.wireOp",EDGE,"E69"),sQuery(id+"F0.wireOp",EDGE,"E70"),sQuery(id+"F0.wireOp",EDGE,"E73"),sQuery(id+"F0.wireOp",EDGE,"E75"),sQuery(id+"F0.wireOp",EDGE,"E76"),sQuery(id+"F0.wireOp",EDGE,"E77"),sQuery(id+"F0.wireOp",EDGE,"E78"),sQuery(id+"F0.wireOp",EDGE,"E79"),sQuery(id+"F0.wireOp",EDGE,"E82"),sQuery(id+"F0.wireOp",EDGE,"E99.1.0.0"),sQuery(id+"F0.wireOp",EDGE,"E99.1.0.1"),sQuery(id+"F0.wireOp",EDGE,"E99.1.0.2"),sQuery(id+"F0.wireOp",EDGE,"E99.1.0.3"),sQuery(id+"F0.wireOp",EDGE,"E99.1.0.4"),sQuery(id+"F0.wireOp",EDGE,"E99.1.0.5"),sQuery(id+"F0.wireOp",EDGE,"E99.1.0.6"),sQuery(id+"F0.wireOp",EDGE,"E99.1.0.7"),sQuery(id+"F0.wireOp",EDGE,"E99.1.0.8"),sQuery(id+"F0.wireOp",EDGE,"E100.0.1.0"),sQuery(id+"F0.wireOp",EDGE,"E100.0.1.1"),sQuery(id+"F0.wireOp",EDGE,"E100.0.1.2"),sQuery(id+"F0.wireOp",EDGE,"E100.0.1.3"),sQuery(id+"F0.wireOp",EDGE,"E100.0.1.4"),sQuery(id+"F0.wireOp",EDGE,"E100.0.1.5"),sQuery(id+"F0.wireOp",EDGE,"E100.0.1.6"),sQuery(id+"F0.wireOp",EDGE,"E100.0.1.7"),sQuery(id+"F0.wireOp",EDGE,"E100.0.1.9"),sQuery(id+"F0.wireOp",EDGE,"E106"),sQuery(id+"F0.wireOp",EDGE,"E107"),sQuery(id+"F0.wireOp",EDGE,"E108"),sQuery(id+"F0.wireOp",EDGE,"E109")])]});
            var Q2;
            {var subQ0=makeQuery(id+"F4.opExtrude","SWEPT_FACE",FACE,{"disambiguationData":[OSD([sQuery(id+"F0.wireOp",EDGE,"E59")])]});Q2=makeQuery(id+"F5.boolean.opBoolean","MERGE",FACE,{"derivedFrom":[subQ0,makeQuery(id+"F5.opPattern","COPY",FACE,{"derivedFrom":subQ0,"instanceName":"1"})]});}
            mirror(context, id + "F7", {"operationType" : NewBodyOperationType.ADD, "entities" : qUnion([Q0, Q1]), "mirrorPlane" : qUnion([Q2])});
        }
        {
            var Q0;
            Q0=makeQuery(id+"F4.opExtrude","SWEPT_BODY",BODY,{"disambiguationData":[OSD([sQuery(id+"F0.wireOp",EDGE,"E16"),sQuery(id+"F0.wireOp",EDGE,"E67"),sQuery(id+"F0.wireOp",EDGE,"E68"),sQuery(id+"F0.wireOp",EDGE,"E69"),sQuery(id+"F0.wireOp",EDGE,"E70"),sQuery(id+"F0.wireOp",EDGE,"E73"),sQuery(id+"F0.wireOp",EDGE,"E75"),sQuery(id+"F0.wireOp",EDGE,"E76"),sQuery(id+"F0.wireOp",EDGE,"E77"),sQuery(id+"F0.wireOp",EDGE,"E78"),sQuery(id+"F0.wireOp",EDGE,"E79"),sQuery(id+"F0.wireOp",EDGE,"E82"),sQuery(id+"F0.wireOp",EDGE,"E99.1.0.0"),sQuery(id+"F0.wireOp",EDGE,"E99.1.0.1"),sQuery(id+"F0.wireOp",EDGE,"E99.1.0.2"),sQuery(id+"F0.wireOp",EDGE,"E99.1.0.3"),sQuery(id+"F0.wireOp",EDGE,"E99.1.0.4"),sQuery(id+"F0.wireOp",EDGE,"E99.1.0.5"),sQuery(id+"F0.wireOp",EDGE,"E99.1.0.6"),sQuery(id+"F0.wireOp",EDGE,"E99.1.0.7"),sQuery(id+"F0.wireOp",EDGE,"E99.1.0.8"),sQuery(id+"F0.wireOp",EDGE,"E100.0.1.0"),sQuery(id+"F0.wireOp",EDGE,"E100.0.1.1"),sQuery(id+"F0.wireOp",EDGE,"E100.0.1.2"),sQuery(id+"F0.wireOp",EDGE,"E100.0.1.3"),sQuery(id+"F0.wireOp",EDGE,"E100.0.1.4"),sQuery(id+"F0.wireOp",EDGE,"E100.0.1.5"),sQuery(id+"F0.wireOp",EDGE,"E100.0.1.6"),sQuery(id+"F0.wireOp",EDGE,"E100.0.1.7"),sQuery(id+"F0.wireOp",EDGE,"E100.0.1.9"),sQuery(id+"F0.wireOp",EDGE,"E106"),sQuery(id+"F0.wireOp",EDGE,"E107"),sQuery(id+"F0.wireOp",EDGE,"E108"),sQuery(id+"F0.wireOp",EDGE,"E109")])]});
            var Q1;
            {var subQ0=makeQuery(id+"F4.opExtrude","SWEPT_FACE",FACE,{"disambiguationData":[OSD([sQuery(id+"F0.wireOp",EDGE,"E16"),sQuery(id+"F0.wireOp",EDGE,"E109")])]});Q1=makeQuery(id+"F7.boolean.opBoolean","MERGE",FACE,{"derivedFrom":[subQ0,makeQuery(id+"F7.opPattern","COPY",FACE,{"derivedFrom":subQ0,"instanceName":"1"})]});}
            mirror(context, id + "F8", {"operationType" : NewBodyOperationType.ADD, "entities" : qUnion([Q0]), "mirrorPlane" : qUnion([Q1])});
        }
        {
            var Q0;
            Q0=makeQuery(id+"F1.imprint","IMPRINT",FACE,{"disambiguationData":[TD([[makeQuery(id+"F1.imprint","IMPRINT",EDGE,{"derivedFrom":sQuery(id+"F1.wireOp",EDGE,"E132")}),1.0]])]});
            var Q1;
            {var subQ13=sQuery(id+"F1.wireOp",EDGE,"E129");Q1=makeQuery(id+"F1.imprint","IMPRINT",FACE,{"disambiguationData":[TD([[makeQuery(id+"F1.imprint","IMPRINT",EDGE,{"derivedFrom":subQ13}),-1.0]])]});}
            var Q2;
            {var subQ4=sQuery(id+"F1.wireOp",EDGE,"E142");Q2=makeQuery(id+"F1.imprint","IMPRINT",FACE,{"disambiguationData":[TD([[makeQuery(id+"F1.imprint","IMPRINT",EDGE,{"derivedFrom":subQ4}),1.0]])]});}
            var Q3;
            Q3=makeQuery(id+"F1.imprint","IMPRINT",FACE,{"disambiguationData":[TD([[makeQuery(id+"F1.imprint","IMPRINT",EDGE,{"derivedFrom":sQuery(id+"F1.wireOp",EDGE,"E148.0.MirrorCS")}),-1.0]])]});
            extrude(context, id + "F9", {"entities" : qUnion([Q0, Q1, Q2, Q3]), "operationType" : NewBodyOperationType.ADD, "depth" : 6.8 * mm});
        }
        {
            var Q0;
            Q0=makeQuery(id+"F4.opExtrude","SWEPT_BODY",BODY,{"disambiguationData":[OSD([sQuery(id+"F0.wireOp",EDGE,"E4"),sQuery(id+"F0.wireOp",EDGE,"E5"),sQuery(id+"F0.wireOp",EDGE,"E39"),sQuery(id+"F0.wireOp",EDGE,"E40"),sQuery(id+"F0.wireOp",EDGE,"E41"),sQuery(id+"F0.wireOp",EDGE,"E42"),sQuery(id+"F0.wireOp",EDGE,"E43"),sQuery(id+"F0.wireOp",EDGE,"E44"),sQuery(id+"F0.wireOp",EDGE,"E45.rect.bottom"),sQuery(id+"F0.wireOp",EDGE,"E45.rect.left"),sQuery(id+"F0.wireOp",EDGE,"E45.rect.right"),sQuery(id+"F0.wireOp",EDGE,"E46"),sQuery(id+"F0.wireOp",EDGE,"E50"),sQuery(id+"F0.wireOp",EDGE,"E51"),sQuery(id+"F0.wireOp",EDGE,"E52"),sQuery(id+"F0.wireOp",EDGE,"E53"),sQuery(id+"F0.wireOp",EDGE,"E54"),sQuery(id+"F0.wireOp",EDGE,"E55"),sQuery(id+"F0.wireOp",EDGE,"E56.rect.bottom"),sQuery(id+"F0.wireOp",EDGE,"E56.rect.top"),sQuery(id+"F0.wireOp",EDGE,"E56.rect.left"),sQuery(id+"F0.wireOp",EDGE,"E57"),sQuery(id+"F0.wireOp",EDGE,"E95.1.0.0"),sQuery(id+"F0.wireOp",EDGE,"E95.1.0.2"),sQuery(id+"F0.wireOp",EDGE,"E95.1.0.3"),sQuery(id+"F0.wireOp",EDGE,"E95.1.0.4"),sQuery(id+"F0.wireOp",EDGE,"E95.1.0.5"),sQuery(id+"F0.wireOp",EDGE,"E95.1.0.6"),sQuery(id+"F0.wireOp",EDGE,"E95.1.0.7"),sQuery(id+"F0.wireOp",EDGE,"E95.1.0.8"),sQuery(id+"F0.wireOp",EDGE,"E95.1.0.9"),sQuery(id+"F0.wireOp",EDGE,"E95.1.0.10"),sQuery(id+"F0.wireOp",EDGE,"E95.1.0.11"),sQuery(id+"F0.wireOp",EDGE,"E95.1.0.13"),sQuery(id+"F0.wireOp",EDGE,"E95.1.0.14"),sQuery(id+"F0.wireOp",EDGE,"E95.1.0.16"),sQuery(id+"F0.wireOp",EDGE,"E95.1.0.17"),sQuery(id+"F0.wireOp",EDGE,"E95.1.0.18"),sQuery(id+"F0.wireOp",EDGE,"E95.1.0.19"),sQuery(id+"F0.wireOp",EDGE,"E95.1.0.20"),sQuery(id+"F0.wireOp",EDGE,"E96.0.1.0"),sQuery(id+"F0.wireOp",EDGE,"E96.0.1.2"),sQuery(id+"F0.wireOp",EDGE,"E96.0.1.3"),sQuery(id+"F0.wireOp",EDGE,"E96.0.1.4"),sQuery(id+"F0.wireOp",EDGE,"E96.0.1.5"),sQuery(id+"F0.wireOp",EDGE,"E96.0.1.6"),sQuery(id+"F0.wireOp",EDGE,"E96.0.1.9"),sQuery(id+"F0.wireOp",EDGE,"E96.0.1.10"),sQuery(id+"F0.wireOp",EDGE,"E96.0.1.11"),sQuery(id+"F0.wireOp",EDGE,"E96.0.1.12"),sQuery(id+"F0.wireOp",EDGE,"E96.0.1.13"),sQuery(id+"F0.wireOp",EDGE,"E96.0.1.14"),sQuery(id+"F0.wireOp",EDGE,"E96.0.1.15"),sQuery(id+"F0.wireOp",EDGE,"E96.0.1.16"),sQuery(id+"F0.wireOp",EDGE,"E96.0.1.17"),sQuery(id+"F0.wireOp",EDGE,"E96.0.1.19"),sQuery(id+"F0.wireOp",EDGE,"E96.0.1.20"),sQuery(id+"F0.wireOp",EDGE,"E96.0.1.22"),sQuery(id+"F0.wireOp",EDGE,"E110"),sQuery(id+"F0.wireOp",EDGE,"E111"),sQuery(id+"F0.wireOp",EDGE,"E112"),sQuery(id+"F0.wireOp",EDGE,"E113")])]});
            var Q1;
            Q1=makeQuery(id+"F4.opExtrude","SWEPT_BODY",BODY,{"disambiguationData":[OSD([sQuery(id+"F0.wireOp",EDGE,"E10"),sQuery(id+"F0.wireOp",EDGE,"E59"),sQuery(id+"F0.wireOp",EDGE,"E60"),sQuery(id+"F0.wireOp",EDGE,"E61"),sQuery(id+"F0.wireOp",EDGE,"E62"),sQuery(id+"F0.wireOp",EDGE,"E63"),sQuery(id+"F0.wireOp",EDGE,"E65"),sQuery(id+"F0.wireOp",EDGE,"E86"),sQuery(id+"F0.wireOp",EDGE,"E87"),sQuery(id+"F0.wireOp",EDGE,"E88"),sQuery(id+"F0.wireOp",EDGE,"E89"),sQuery(id+"F0.wireOp",EDGE,"E90"),sQuery(id+"F0.wireOp",EDGE,"E91"),sQuery(id+"F0.wireOp",EDGE,"E92.rect.bottom"),sQuery(id+"F0.wireOp",EDGE,"E92.rect.left"),sQuery(id+"F0.wireOp",EDGE,"E92.rect.right"),sQuery(id+"F0.wireOp",EDGE,"E93"),sQuery(id+"F0.wireOp",EDGE,"E97.1.0.0"),sQuery(id+"F0.wireOp",EDGE,"E97.1.0.1"),sQuery(id+"F0.wireOp",EDGE,"E97.1.0.2"),sQuery(id+"F0.wireOp",EDGE,"E97.1.0.3"),sQuery(id+"F0.wireOp",EDGE,"E97.1.0.4"),sQuery(id+"F0.wireOp",EDGE,"E97.1.0.5"),sQuery(id+"F0.wireOp",EDGE,"E97.1.0.6"),sQuery(id+"F0.wireOp",EDGE,"E97.1.0.7"),sQuery(id+"F0.wireOp",EDGE,"E97.1.0.8"),sQuery(id+"F0.wireOp",EDGE,"E98.0.1.1"),sQuery(id+"F0.wireOp",EDGE,"E98.0.1.2"),sQuery(id+"F0.wireOp",EDGE,"E98.0.1.3"),sQuery(id+"F0.wireOp",EDGE,"E98.0.1.4"),sQuery(id+"F0.wireOp",EDGE,"E98.0.1.6"),sQuery(id+"F0.wireOp",EDGE,"E98.0.1.7"),sQuery(id+"F0.wireOp",EDGE,"E98.0.1.8"),sQuery(id+"F0.wireOp",EDGE,"E98.0.1.9"),sQuery(id+"F0.wireOp",EDGE,"E98.0.1.10"),sQuery(id+"F0.wireOp",EDGE,"E98.0.1.11"),sQuery(id+"F0.wireOp",EDGE,"E98.0.1.12"),sQuery(id+"F0.wireOp",EDGE,"E98.0.1.13"),sQuery(id+"F0.wireOp",EDGE,"E98.0.1.16"),sQuery(id+"F0.wireOp",EDGE,"E98.0.1.17"),sQuery(id+"F0.wireOp",EDGE,"E98.0.1.18"),sQuery(id+"F0.wireOp",EDGE,"E98.0.1.19"),sQuery(id+"F0.wireOp",EDGE,"E98.0.1.20"),sQuery(id+"F0.wireOp",EDGE,"E98.0.1.21"),sQuery(id+"F0.wireOp",EDGE,"E101"),sQuery(id+"F0.wireOp",EDGE,"E102"),sQuery(id+"F0.wireOp",EDGE,"E103"),sQuery(id+"F0.wireOp",EDGE,"E104"),sQuery(id+"F0.wireOp",EDGE,"E105")])]});
            var Q2;
            Q2=makeQuery(id+"F4.opExtrude","SWEPT_BODY",BODY,{"disambiguationData":[OSD([sQuery(id+"F0.wireOp",EDGE,"E16"),sQuery(id+"F0.wireOp",EDGE,"E67"),sQuery(id+"F0.wireOp",EDGE,"E68"),sQuery(id+"F0.wireOp",EDGE,"E69"),sQuery(id+"F0.wireOp",EDGE,"E70"),sQuery(id+"F0.wireOp",EDGE,"E73"),sQuery(id+"F0.wireOp",EDGE,"E75"),sQuery(id+"F0.wireOp",EDGE,"E76"),sQuery(id+"F0.wireOp",EDGE,"E77"),sQuery(id+"F0.wireOp",EDGE,"E78"),sQuery(id+"F0.wireOp",EDGE,"E79"),sQuery(id+"F0.wireOp",EDGE,"E82"),sQuery(id+"F0.wireOp",EDGE,"E99.1.0.0"),sQuery(id+"F0.wireOp",EDGE,"E99.1.0.1"),sQuery(id+"F0.wireOp",EDGE,"E99.1.0.2"),sQuery(id+"F0.wireOp",EDGE,"E99.1.0.3"),sQuery(id+"F0.wireOp",EDGE,"E99.1.0.4"),sQuery(id+"F0.wireOp",EDGE,"E99.1.0.5"),sQuery(id+"F0.wireOp",EDGE,"E99.1.0.6"),sQuery(id+"F0.wireOp",EDGE,"E99.1.0.7"),sQuery(id+"F0.wireOp",EDGE,"E99.1.0.8"),sQuery(id+"F0.wireOp",EDGE,"E100.0.1.0"),sQuery(id+"F0.wireOp",EDGE,"E100.0.1.1"),sQuery(id+"F0.wireOp",EDGE,"E100.0.1.2"),sQuery(id+"F0.wireOp",EDGE,"E100.0.1.3"),sQuery(id+"F0.wireOp",EDGE,"E100.0.1.4"),sQuery(id+"F0.wireOp",EDGE,"E100.0.1.5"),sQuery(id+"F0.wireOp",EDGE,"E100.0.1.6"),sQuery(id+"F0.wireOp",EDGE,"E100.0.1.7"),sQuery(id+"F0.wireOp",EDGE,"E100.0.1.9"),sQuery(id+"F0.wireOp",EDGE,"E106"),sQuery(id+"F0.wireOp",EDGE,"E107"),sQuery(id+"F0.wireOp",EDGE,"E108"),sQuery(id+"F0.wireOp",EDGE,"E109")])]});
            transform(context, id + "F10", {"entities" : qUnion([Q0, Q1, Q2]), "transformType" : TransformType.TRANSLATION_3D, "dx" : 0 * mm, "dy" : 0 * mm, "dz" : 10 * mm, "makeCopy" : true});
        }
        {
            var Q0;
            Q0 = qSketchRegion(id + "F2", true);
            extrude(context, id + "F11", {"entities" : qUnion([Q0]), "operationType" : NewBodyOperationType.REMOVE, "endBound" : BoundingType.THROUGH_ALL, "depth" : 25 * mm});
        }
        {
            var Q0;
            Q0 = qSketchRegion(id + "F3", true);
            extrude(context, id + "F12", {"entities" : qUnion([Q0]), "operationType" : NewBodyOperationType.REMOVE, "endBound" : BoundingType.THROUGH_ALL, "depth" : 25 * mm});
        }
    });
